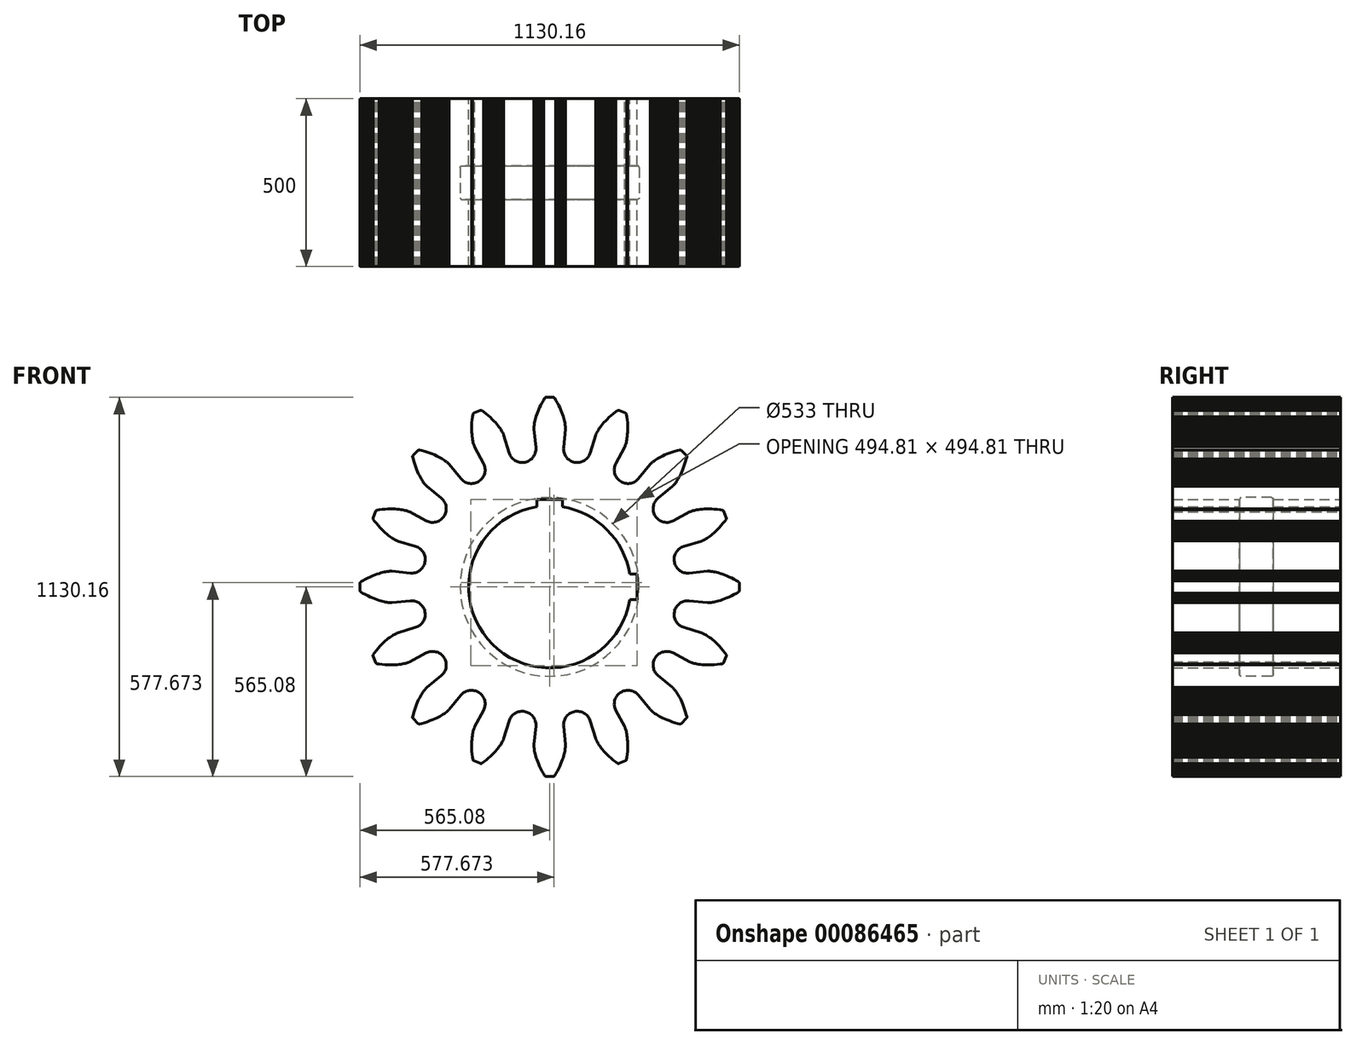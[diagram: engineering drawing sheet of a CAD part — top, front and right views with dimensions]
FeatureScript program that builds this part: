
annotation { "Feature Type Name" : "Feature", "Feature Type Description" : "" }
export const myFeature = defineFeature(function(context is Context, id is Id, definition is map)
    precondition{}
    {
        {
            var Q0;
            Q0=qCreatedBy(makeId("Front.planeOp"),FACE);
            var sketch = newSketch(context, id + "F0", { "sketchPlane" : qUnion([Q0])});
            skLineSegment(sketch, "E0", {"start": v(-415.34, 41.32) * mm, "end": v(-470.23, 46.78) * mm});
            skLineSegment(sketch, "E1", {"start": v(-470.23, 46.78) * mm, "end": v(-471.28, 46.9) * mm});
            skLineSegment(sketch, "E2", {"start": v(-471.28, 46.9) * mm, "end": v(-472.46, 46.9) * mm});
            skLineSegment(sketch, "E3", {"start": v(-472.46, 46.9) * mm, "end": v(-474.07, 46.85) * mm});
            skLineSegment(sketch, "E4", {"start": v(-474.07, 46.85) * mm, "end": v(-476.11, 46.73) * mm});
            skLineSegment(sketch, "E5", {"start": v(-476.11, 46.73) * mm, "end": v(-478.7, 46.56) * mm});
            skLineSegment(sketch, "E6", {"start": v(-478.7, 46.56) * mm, "end": v(-481.62, 46.2) * mm});
            skLineSegment(sketch, "E7", {"start": v(-481.62, 46.2) * mm, "end": v(-485.08, 45.8) * mm});
            skLineSegment(sketch, "E8", {"start": v(-485.08, 45.8) * mm, "end": v(-489, 45.12) * mm});
            skLineSegment(sketch, "E9", {"start": v(-489, 45.12) * mm, "end": v(-493.25, 44.26) * mm});
            skLineSegment(sketch, "E10", {"start": v(-493.25, 44.26) * mm, "end": v(-497.96, 43.13) * mm});
            skLineSegment(sketch, "E11", {"start": v(-497.96, 43.13) * mm, "end": v(-503.12, 41.82) * mm});
            skLineSegment(sketch, "E12", {"start": v(-503.12, 41.82) * mm, "end": v(-508.63, 40.13) * mm});
            skLineSegment(sketch, "E13", {"start": v(-508.63, 40.13) * mm, "end": v(-514.5, 38.14) * mm});
            skLineSegment(sketch, "E14", {"start": v(-514.5, 38.14) * mm, "end": v(-520.83, 35.78) * mm});
            skLineSegment(sketch, "E15", {"start": v(-520.83, 35.78) * mm, "end": v(-527.4, 33.12) * mm});
            skLineSegment(sketch, "E16", {"start": v(-527.4, 33.12) * mm, "end": v(-534.34, 30.07) * mm});
            skLineSegment(sketch, "E17", {"start": v(-534.34, 30.07) * mm, "end": v(-541.63, 26.62) * mm});
            skLineSegment(sketch, "E18", {"start": v(-541.63, 26.62) * mm, "end": v(-549.19, 22.67) * mm});
            skLineSegment(sketch, "E19", {"start": v(-549.19, 22.67) * mm, "end": v(-557, 18.31) * mm});
            skLineSegment(sketch, "E20", {"start": v(-557, 18.31) * mm, "end": v(-562.5, 15) * mm});
            skArc(sketch, "E21", {"start": v(-562.5, 15) * mm, "mid": v(-564.39, 13.06) * mm, "end": v(-565.08, 10.44) * mm});
            skLineSegment(sketch, "E22", {"start": v(-565.08, 10.44) * mm, "end": v(-565.08, -10.44) * mm});
            skArc(sketch, "E23", {"start": v(-565.08, -10.44) * mm, "mid": v(-564.39, -13.06) * mm, "end": v(-562.5, -15) * mm});
            skLineSegment(sketch, "E24", {"start": v(-562.5, -15) * mm, "end": v(-557, -18.31) * mm});
            skLineSegment(sketch, "E25", {"start": v(-557, -18.31) * mm, "end": v(-549.19, -22.67) * mm});
            skLineSegment(sketch, "E26", {"start": v(-549.19, -22.67) * mm, "end": v(-541.63, -26.62) * mm});
            skLineSegment(sketch, "E27", {"start": v(-541.63, -26.62) * mm, "end": v(-534.34, -30.07) * mm});
            skLineSegment(sketch, "E28", {"start": v(-534.34, -30.07) * mm, "end": v(-527.4, -33.12) * mm});
            skLineSegment(sketch, "E29", {"start": v(-527.4, -33.12) * mm, "end": v(-520.83, -35.78) * mm});
            skLineSegment(sketch, "E30", {"start": v(-520.83, -35.78) * mm, "end": v(-514.5, -38.14) * mm});
            skLineSegment(sketch, "E31", {"start": v(-514.5, -38.14) * mm, "end": v(-508.63, -40.13) * mm});
            skLineSegment(sketch, "E32", {"start": v(-508.63, -40.13) * mm, "end": v(-503.12, -41.82) * mm});
            skLineSegment(sketch, "E33", {"start": v(-503.12, -41.82) * mm, "end": v(-497.96, -43.13) * mm});
            skLineSegment(sketch, "E34", {"start": v(-497.96, -43.13) * mm, "end": v(-493.25, -44.26) * mm});
            skLineSegment(sketch, "E35", {"start": v(-493.25, -44.26) * mm, "end": v(-489, -45.12) * mm});
            skLineSegment(sketch, "E36", {"start": v(-489, -45.12) * mm, "end": v(-485.08, -45.8) * mm});
            skLineSegment(sketch, "E37", {"start": v(-485.08, -45.8) * mm, "end": v(-481.62, -46.2) * mm});
            skLineSegment(sketch, "E38", {"start": v(-481.62, -46.2) * mm, "end": v(-478.7, -46.56) * mm});
            skLineSegment(sketch, "E39", {"start": v(-478.7, -46.56) * mm, "end": v(-476.11, -46.73) * mm});
            skLineSegment(sketch, "E40", {"start": v(-476.11, -46.73) * mm, "end": v(-474.07, -46.85) * mm});
            skLineSegment(sketch, "E41", {"start": v(-474.07, -46.85) * mm, "end": v(-472.46, -46.9) * mm});
            skLineSegment(sketch, "E42", {"start": v(-472.46, -46.9) * mm, "end": v(-471.28, -46.9) * mm});
            skLineSegment(sketch, "E43", {"start": v(-471.28, -46.9) * mm, "end": v(-470.23, -46.78) * mm});
            skLineSegment(sketch, "E44", {"start": v(-470.23, -46.78) * mm, "end": v(-415.34, -41.32) * mm});
            skLineSegment(sketch, "E45", {"start": v(415.34, -41.32) * mm, "end": v(470.23, -46.78) * mm});
            skLineSegment(sketch, "E46", {"start": v(470.23, -46.78) * mm, "end": v(471.28, -46.9) * mm});
            skLineSegment(sketch, "E47", {"start": v(471.28, -46.9) * mm, "end": v(472.46, -46.9) * mm});
            skLineSegment(sketch, "E48", {"start": v(472.46, -46.9) * mm, "end": v(474.07, -46.85) * mm});
            skLineSegment(sketch, "E49", {"start": v(474.07, -46.85) * mm, "end": v(476.11, -46.73) * mm});
            skLineSegment(sketch, "E50", {"start": v(476.11, -46.73) * mm, "end": v(478.7, -46.56) * mm});
            skLineSegment(sketch, "E51", {"start": v(478.7, -46.56) * mm, "end": v(481.62, -46.2) * mm});
            skLineSegment(sketch, "E52", {"start": v(481.62, -46.2) * mm, "end": v(485.08, -45.8) * mm});
            skLineSegment(sketch, "E53", {"start": v(485.08, -45.8) * mm, "end": v(489, -45.12) * mm});
            skLineSegment(sketch, "E54", {"start": v(489, -45.12) * mm, "end": v(493.25, -44.26) * mm});
            skLineSegment(sketch, "E55", {"start": v(493.25, -44.26) * mm, "end": v(497.96, -43.13) * mm});
            skLineSegment(sketch, "E56", {"start": v(497.96, -43.13) * mm, "end": v(503.12, -41.82) * mm});
            skLineSegment(sketch, "E57", {"start": v(503.12, -41.82) * mm, "end": v(508.63, -40.13) * mm});
            skLineSegment(sketch, "E58", {"start": v(508.63, -40.13) * mm, "end": v(514.5, -38.14) * mm});
            skLineSegment(sketch, "E59", {"start": v(514.5, -38.14) * mm, "end": v(520.83, -35.78) * mm});
            skLineSegment(sketch, "E60", {"start": v(520.83, -35.78) * mm, "end": v(527.4, -33.12) * mm});
            skLineSegment(sketch, "E61", {"start": v(527.4, -33.12) * mm, "end": v(534.34, -30.07) * mm});
            skLineSegment(sketch, "E62", {"start": v(534.34, -30.07) * mm, "end": v(541.63, -26.62) * mm});
            skLineSegment(sketch, "E63", {"start": v(541.63, -26.62) * mm, "end": v(549.19, -22.67) * mm});
            skLineSegment(sketch, "E64", {"start": v(549.19, -22.67) * mm, "end": v(557, -18.31) * mm});
            skLineSegment(sketch, "E65", {"start": v(557, -18.31) * mm, "end": v(562.5, -15) * mm});
            skArc(sketch, "E66", {"start": v(562.5, -15) * mm, "mid": v(564.39, -13.06) * mm, "end": v(565.08, -10.44) * mm});
            skLineSegment(sketch, "E67", {"start": v(565.08, -10.44) * mm, "end": v(565.08, 10.44) * mm});
            skArc(sketch, "E68", {"start": v(565.08, 10.44) * mm, "mid": v(564.39, 13.06) * mm, "end": v(562.5, 15) * mm});
            skLineSegment(sketch, "E69", {"start": v(562.5, 15) * mm, "end": v(557, 18.31) * mm});
            skLineSegment(sketch, "E70", {"start": v(557, 18.31) * mm, "end": v(549.19, 22.67) * mm});
            skLineSegment(sketch, "E71", {"start": v(549.19, 22.67) * mm, "end": v(541.63, 26.62) * mm});
            skLineSegment(sketch, "E72", {"start": v(541.63, 26.62) * mm, "end": v(534.34, 30.07) * mm});
            skLineSegment(sketch, "E73", {"start": v(534.34, 30.07) * mm, "end": v(527.4, 33.12) * mm});
            skLineSegment(sketch, "E74", {"start": v(527.4, 33.12) * mm, "end": v(520.83, 35.78) * mm});
            skLineSegment(sketch, "E75", {"start": v(520.83, 35.78) * mm, "end": v(514.5, 38.14) * mm});
            skLineSegment(sketch, "E76", {"start": v(514.5, 38.14) * mm, "end": v(508.63, 40.13) * mm});
            skLineSegment(sketch, "E77", {"start": v(508.63, 40.13) * mm, "end": v(503.12, 41.82) * mm});
            skLineSegment(sketch, "E78", {"start": v(503.12, 41.82) * mm, "end": v(497.96, 43.13) * mm});
            skLineSegment(sketch, "E79", {"start": v(497.96, 43.13) * mm, "end": v(493.25, 44.26) * mm});
            skLineSegment(sketch, "E80", {"start": v(493.25, 44.26) * mm, "end": v(489, 45.12) * mm});
            skLineSegment(sketch, "E81", {"start": v(489, 45.12) * mm, "end": v(485.08, 45.8) * mm});
            skLineSegment(sketch, "E82", {"start": v(485.08, 45.8) * mm, "end": v(481.62, 46.2) * mm});
            skLineSegment(sketch, "E83", {"start": v(481.62, 46.2) * mm, "end": v(478.7, 46.56) * mm});
            skLineSegment(sketch, "E84", {"start": v(478.7, 46.56) * mm, "end": v(476.11, 46.73) * mm});
            skLineSegment(sketch, "E85", {"start": v(476.11, 46.73) * mm, "end": v(474.07, 46.85) * mm});
            skLineSegment(sketch, "E86", {"start": v(474.07, 46.85) * mm, "end": v(472.46, 46.9) * mm});
            skLineSegment(sketch, "E87", {"start": v(472.46, 46.9) * mm, "end": v(471.28, 46.9) * mm});
            skLineSegment(sketch, "E88", {"start": v(471.28, 46.9) * mm, "end": v(470.23, 46.78) * mm});
            skLineSegment(sketch, "E89", {"start": v(470.23, 46.78) * mm, "end": v(415.34, 41.32) * mm});
            skArc(sketch, "E90", {"start": v(371.58, -74.15) * mm, "mid": v(376.56, -102.85) * mm, "end": v(399.54, -120.77) * mm});
            skLineSegment(sketch, "E91", {"start": v(367.91, -197.12) * mm, "end": v(416.53, -223.17) * mm});
            skLineSegment(sketch, "E92", {"start": v(416.53, -223.17) * mm, "end": v(417.47, -223.67) * mm});
            skLineSegment(sketch, "E93", {"start": v(417.47, -223.67) * mm, "end": v(418.55, -224.13) * mm});
            skLineSegment(sketch, "E94", {"start": v(418.55, -224.13) * mm, "end": v(420.06, -224.7) * mm});
            skLineSegment(sketch, "E95", {"start": v(420.06, -224.7) * mm, "end": v(421.99, -225.37) * mm});
            skLineSegment(sketch, "E96", {"start": v(421.99, -225.37) * mm, "end": v(424.44, -226.2) * mm});
            skLineSegment(sketch, "E97", {"start": v(424.44, -226.2) * mm, "end": v(427.27, -227) * mm});
            skLineSegment(sketch, "E98", {"start": v(427.27, -227) * mm, "end": v(430.63, -227.95) * mm});
            skLineSegment(sketch, "E99", {"start": v(430.63, -227.95) * mm, "end": v(434.5, -228.82) * mm});
            skLineSegment(sketch, "E100", {"start": v(434.5, -228.82) * mm, "end": v(438.77, -229.65) * mm});
            skLineSegment(sketch, "E101", {"start": v(438.77, -229.65) * mm, "end": v(443.55, -230.4) * mm});
            skLineSegment(sketch, "E102", {"start": v(443.55, -230.4) * mm, "end": v(448.82, -231.18) * mm});
            skLineSegment(sketch, "E103", {"start": v(448.82, -231.18) * mm, "end": v(454.56, -231.72) * mm});
            skLineSegment(sketch, "E104", {"start": v(454.56, -231.72) * mm, "end": v(460.74, -232.13) * mm});
            skLineSegment(sketch, "E105", {"start": v(460.74, -232.13) * mm, "end": v(467.5, -232.37) * mm});
            skLineSegment(sketch, "E106", {"start": v(467.5, -232.37) * mm, "end": v(474.58, -232.43) * mm});
            skLineSegment(sketch, "E107", {"start": v(474.58, -232.43) * mm, "end": v(482.16, -232.26) * mm});
            skLineSegment(sketch, "E108", {"start": v(482.16, -232.26) * mm, "end": v(490.21, -231.87) * mm});
            skLineSegment(sketch, "E109", {"start": v(490.21, -231.87) * mm, "end": v(498.7, -231.1) * mm});
            skLineSegment(sketch, "E110", {"start": v(498.7, -231.1) * mm, "end": v(507.6, -230.07) * mm});
            skLineSegment(sketch, "E111", {"start": v(507.6, -230.07) * mm, "end": v(513.94, -229.12) * mm});
            skArc(sketch, "E112", {"start": v(513.94, -229.12) * mm, "mid": v(516.43, -228.05) * mm, "end": v(518.07, -225.9) * mm});
            skLineSegment(sketch, "E113", {"start": v(518.07, -225.9) * mm, "end": v(526.06, -206.6) * mm});
            skArc(sketch, "E114", {"start": v(526.06, -206.6) * mm, "mid": v(526.42, -203.92) * mm, "end": v(525.42, -201.4) * mm});
            skLineSegment(sketch, "E115", {"start": v(525.42, -201.4) * mm, "end": v(521.6, -196.24) * mm});
            skLineSegment(sketch, "E116", {"start": v(521.6, -196.24) * mm, "end": v(516.06, -189.22) * mm});
            skLineSegment(sketch, "E117", {"start": v(516.06, -189.22) * mm, "end": v(510.59, -182.68) * mm});
            skLineSegment(sketch, "E118", {"start": v(510.59, -182.68) * mm, "end": v(505.17, -176.7) * mm});
            skLineSegment(sketch, "E119", {"start": v(505.17, -176.7) * mm, "end": v(499.93, -171.23) * mm});
            skLineSegment(sketch, "E120", {"start": v(499.93, -171.23) * mm, "end": v(494.88, -166.26) * mm});
            skLineSegment(sketch, "E121", {"start": v(494.88, -166.26) * mm, "end": v(489.93, -161.65) * mm});
            skLineSegment(sketch, "E122", {"start": v(489.93, -161.65) * mm, "end": v(485.27, -157.57) * mm});
            skLineSegment(sketch, "E123", {"start": v(485.27, -157.57) * mm, "end": v(480.83, -153.9) * mm});
            skLineSegment(sketch, "E124", {"start": v(480.83, -153.9) * mm, "end": v(476.56, -150.72) * mm});
            skLineSegment(sketch, "E125", {"start": v(476.56, -150.72) * mm, "end": v(472.65, -147.86) * mm});
            skLineSegment(sketch, "E126", {"start": v(472.65, -147.86) * mm, "end": v(469.04, -145.44) * mm});
            skLineSegment(sketch, "E127", {"start": v(469.04, -145.44) * mm, "end": v(465.68, -143.32) * mm});
            skLineSegment(sketch, "E128", {"start": v(465.68, -143.32) * mm, "end": v(462.64, -141.62) * mm});
            skLineSegment(sketch, "E129", {"start": v(462.64, -141.62) * mm, "end": v(460.07, -140.17) * mm});
            skLineSegment(sketch, "E130", {"start": v(460.07, -140.17) * mm, "end": v(457.75, -139.03) * mm});
            skLineSegment(sketch, "E131", {"start": v(457.75, -139.03) * mm, "end": v(455.91, -138.14) * mm});
            skLineSegment(sketch, "E132", {"start": v(455.91, -138.14) * mm, "end": v(454.44, -137.47) * mm});
            skLineSegment(sketch, "E133", {"start": v(454.44, -137.47) * mm, "end": v(453.35, -137.03) * mm});
            skLineSegment(sketch, "E134", {"start": v(453.35, -137.03) * mm, "end": v(452.34, -136.72) * mm});
            skLineSegment(sketch, "E135", {"start": v(452.34, -136.72) * mm, "end": v(399.54, -120.77) * mm});
            skLineSegment(sketch, "E136", {"start": v(264.47, -322.91) * mm, "end": v(299.42, -365.58) * mm});
            skLineSegment(sketch, "E137", {"start": v(299.42, -365.58) * mm, "end": v(300.1, -366.4) * mm});
            skLineSegment(sketch, "E138", {"start": v(300.1, -366.4) * mm, "end": v(300.92, -367.24) * mm});
            skLineSegment(sketch, "E139", {"start": v(300.92, -367.24) * mm, "end": v(302.1, -368.34) * mm});
            skLineSegment(sketch, "E140", {"start": v(302.1, -368.34) * mm, "end": v(303.62, -369.7) * mm});
            skLineSegment(sketch, "E141", {"start": v(303.62, -369.7) * mm, "end": v(305.57, -371.41) * mm});
            skLineSegment(sketch, "E142", {"start": v(305.57, -371.41) * mm, "end": v(307.88, -373.23) * mm});
            skLineSegment(sketch, "E143", {"start": v(307.88, -373.23) * mm, "end": v(310.62, -375.4) * mm});
            skLineSegment(sketch, "E144", {"start": v(310.62, -375.4) * mm, "end": v(313.87, -377.68) * mm});
            skLineSegment(sketch, "E145", {"start": v(313.87, -377.68) * mm, "end": v(317.48, -380.08) * mm});
            skLineSegment(sketch, "E146", {"start": v(317.48, -380.08) * mm, "end": v(321.62, -382.61) * mm});
            skLineSegment(sketch, "E147", {"start": v(321.62, -382.61) * mm, "end": v(326.19, -385.33) * mm});
            skLineSegment(sketch, "E148", {"start": v(326.19, -385.33) * mm, "end": v(331.28, -388.03) * mm});
            skLineSegment(sketch, "E149", {"start": v(331.28, -388.03) * mm, "end": v(336.83, -390.78) * mm});
            skLineSegment(sketch, "E150", {"start": v(336.83, -390.78) * mm, "end": v(342.98, -393.58) * mm});
            skLineSegment(sketch, "E151", {"start": v(342.98, -393.58) * mm, "end": v(349.51, -396.35) * mm});
            skLineSegment(sketch, "E152", {"start": v(349.51, -396.35) * mm, "end": v(356.57, -399.1) * mm});
            skLineSegment(sketch, "E153", {"start": v(356.57, -399.1) * mm, "end": v(364.17, -401.81) * mm});
            skLineSegment(sketch, "E154", {"start": v(364.17, -401.81) * mm, "end": v(372.3, -404.36) * mm});
            skLineSegment(sketch, "E155", {"start": v(372.3, -404.36) * mm, "end": v(380.9, -406.8) * mm});
            skLineSegment(sketch, "E156", {"start": v(380.9, -406.8) * mm, "end": v(387.14, -408.35) * mm});
            skArc(sketch, "E157", {"start": v(387.14, -408.35) * mm, "mid": v(389.85, -408.32) * mm, "end": v(392.18, -406.95) * mm});
            skLineSegment(sketch, "E158", {"start": v(392.18, -406.95) * mm, "end": v(406.95, -392.18) * mm});
            skArc(sketch, "E159", {"start": v(406.95, -392.18) * mm, "mid": v(408.32, -389.85) * mm, "end": v(408.35, -387.14) * mm});
            skLineSegment(sketch, "E160", {"start": v(408.35, -387.14) * mm, "end": v(406.8, -380.9) * mm});
            skLineSegment(sketch, "E161", {"start": v(406.8, -380.9) * mm, "end": v(404.36, -372.3) * mm});
            skLineSegment(sketch, "E162", {"start": v(404.36, -372.3) * mm, "end": v(401.81, -364.17) * mm});
            skLineSegment(sketch, "E163", {"start": v(401.81, -364.17) * mm, "end": v(399.1, -356.57) * mm});
            skLineSegment(sketch, "E164", {"start": v(399.1, -356.57) * mm, "end": v(396.35, -349.51) * mm});
            skLineSegment(sketch, "E165", {"start": v(396.35, -349.51) * mm, "end": v(393.58, -342.98) * mm});
            skLineSegment(sketch, "E166", {"start": v(393.58, -342.98) * mm, "end": v(390.78, -336.83) * mm});
            skLineSegment(sketch, "E167", {"start": v(390.78, -336.83) * mm, "end": v(388.03, -331.28) * mm});
            skLineSegment(sketch, "E168", {"start": v(388.03, -331.28) * mm, "end": v(385.33, -326.19) * mm});
            skLineSegment(sketch, "E169", {"start": v(385.33, -326.19) * mm, "end": v(382.61, -321.62) * mm});
            skLineSegment(sketch, "E170", {"start": v(382.61, -321.62) * mm, "end": v(380.08, -317.48) * mm});
            skLineSegment(sketch, "E171", {"start": v(380.08, -317.48) * mm, "end": v(377.68, -313.87) * mm});
            skLineSegment(sketch, "E172", {"start": v(377.68, -313.87) * mm, "end": v(375.4, -310.62) * mm});
            skLineSegment(sketch, "E173", {"start": v(375.4, -310.62) * mm, "end": v(373.23, -307.88) * mm});
            skLineSegment(sketch, "E174", {"start": v(373.23, -307.88) * mm, "end": v(371.41, -305.57) * mm});
            skLineSegment(sketch, "E175", {"start": v(371.41, -305.57) * mm, "end": v(369.7, -303.62) * mm});
            skLineSegment(sketch, "E176", {"start": v(369.7, -303.62) * mm, "end": v(368.34, -302.1) * mm});
            skLineSegment(sketch, "E177", {"start": v(368.34, -302.1) * mm, "end": v(367.24, -300.92) * mm});
            skLineSegment(sketch, "E178", {"start": v(367.24, -300.92) * mm, "end": v(366.4, -300.1) * mm});
            skLineSegment(sketch, "E179", {"start": v(366.4, -300.1) * mm, "end": v(365.58, -299.42) * mm});
            skLineSegment(sketch, "E180", {"start": v(365.58, -299.42) * mm, "end": v(322.91, -264.47) * mm});
            skArc(sketch, "E181", {"start": v(415.34, -41.32) * mm, "mid": v(387.26, -49.08) * mm, "end": v(371.67, -73.7) * mm});
            skArc(sketch, "E182", {"start": v(120.77, -399.54) * mm, "mid": v(102.85, -376.56) * mm, "end": v(74.15, -371.58) * mm});
            skLineSegment(sketch, "E183", {"start": v(120.77, -399.54) * mm, "end": v(136.72, -452.34) * mm});
            skLineSegment(sketch, "E184", {"start": v(136.72, -452.34) * mm, "end": v(137.03, -453.35) * mm});
            skLineSegment(sketch, "E185", {"start": v(137.03, -453.35) * mm, "end": v(137.47, -454.44) * mm});
            skLineSegment(sketch, "E186", {"start": v(137.47, -454.44) * mm, "end": v(138.14, -455.91) * mm});
            skLineSegment(sketch, "E187", {"start": v(138.14, -455.91) * mm, "end": v(139.03, -457.75) * mm});
            skLineSegment(sketch, "E188", {"start": v(139.03, -457.75) * mm, "end": v(140.17, -460.07) * mm});
            skLineSegment(sketch, "E189", {"start": v(140.17, -460.07) * mm, "end": v(141.62, -462.64) * mm});
            skLineSegment(sketch, "E190", {"start": v(141.62, -462.64) * mm, "end": v(143.32, -465.68) * mm});
            skLineSegment(sketch, "E191", {"start": v(143.32, -465.68) * mm, "end": v(145.44, -469.04) * mm});
            skLineSegment(sketch, "E192", {"start": v(145.44, -469.04) * mm, "end": v(147.86, -472.65) * mm});
            skLineSegment(sketch, "E193", {"start": v(147.86, -472.65) * mm, "end": v(150.72, -476.56) * mm});
            skLineSegment(sketch, "E194", {"start": v(150.72, -476.56) * mm, "end": v(153.9, -480.83) * mm});
            skLineSegment(sketch, "E195", {"start": v(153.9, -480.83) * mm, "end": v(157.57, -485.27) * mm});
            skLineSegment(sketch, "E196", {"start": v(157.57, -485.27) * mm, "end": v(161.65, -489.93) * mm});
            skLineSegment(sketch, "E197", {"start": v(161.65, -489.93) * mm, "end": v(166.26, -494.88) * mm});
            skLineSegment(sketch, "E198", {"start": v(166.26, -494.88) * mm, "end": v(171.23, -499.93) * mm});
            skLineSegment(sketch, "E199", {"start": v(171.23, -499.93) * mm, "end": v(176.7, -505.17) * mm});
            skLineSegment(sketch, "E200", {"start": v(176.7, -505.17) * mm, "end": v(182.68, -510.59) * mm});
            skLineSegment(sketch, "E201", {"start": v(182.68, -510.59) * mm, "end": v(189.22, -516.06) * mm});
            skLineSegment(sketch, "E202", {"start": v(189.22, -516.06) * mm, "end": v(196.24, -521.6) * mm});
            skLineSegment(sketch, "E203", {"start": v(196.24, -521.6) * mm, "end": v(201.4, -525.42) * mm});
            skArc(sketch, "E204", {"start": v(201.4, -525.42) * mm, "mid": v(203.92, -526.42) * mm, "end": v(206.6, -526.06) * mm});
            skLineSegment(sketch, "E205", {"start": v(206.6, -526.06) * mm, "end": v(225.9, -518.07) * mm});
            skArc(sketch, "E206", {"start": v(225.9, -518.07) * mm, "mid": v(228.05, -516.43) * mm, "end": v(229.12, -513.94) * mm});
            skLineSegment(sketch, "E207", {"start": v(229.12, -513.94) * mm, "end": v(230.07, -507.6) * mm});
            skLineSegment(sketch, "E208", {"start": v(230.07, -507.6) * mm, "end": v(231.1, -498.7) * mm});
            skLineSegment(sketch, "E209", {"start": v(231.1, -498.7) * mm, "end": v(231.87, -490.21) * mm});
            skLineSegment(sketch, "E210", {"start": v(231.87, -490.21) * mm, "end": v(232.26, -482.16) * mm});
            skLineSegment(sketch, "E211", {"start": v(232.26, -482.16) * mm, "end": v(232.43, -474.58) * mm});
            skLineSegment(sketch, "E212", {"start": v(232.43, -474.58) * mm, "end": v(232.37, -467.5) * mm});
            skLineSegment(sketch, "E213", {"start": v(232.37, -467.5) * mm, "end": v(232.13, -460.74) * mm});
            skLineSegment(sketch, "E214", {"start": v(232.13, -460.74) * mm, "end": v(231.72, -454.56) * mm});
            skLineSegment(sketch, "E215", {"start": v(231.72, -454.56) * mm, "end": v(231.18, -448.82) * mm});
            skLineSegment(sketch, "E216", {"start": v(231.18, -448.82) * mm, "end": v(230.4, -443.55) * mm});
            skLineSegment(sketch, "E217", {"start": v(230.4, -443.55) * mm, "end": v(229.65, -438.77) * mm});
            skLineSegment(sketch, "E218", {"start": v(229.65, -438.77) * mm, "end": v(228.82, -434.5) * mm});
            skLineSegment(sketch, "E219", {"start": v(228.82, -434.5) * mm, "end": v(227.95, -430.63) * mm});
            skLineSegment(sketch, "E220", {"start": v(227.95, -430.63) * mm, "end": v(227, -427.27) * mm});
            skLineSegment(sketch, "E221", {"start": v(227, -427.27) * mm, "end": v(226.2, -424.44) * mm});
            skLineSegment(sketch, "E222", {"start": v(226.2, -424.44) * mm, "end": v(225.37, -421.99) * mm});
            skLineSegment(sketch, "E223", {"start": v(225.37, -421.99) * mm, "end": v(224.7, -420.06) * mm});
            skLineSegment(sketch, "E224", {"start": v(224.7, -420.06) * mm, "end": v(224.13, -418.55) * mm});
            skLineSegment(sketch, "E225", {"start": v(224.13, -418.55) * mm, "end": v(223.67, -417.47) * mm});
            skLineSegment(sketch, "E226", {"start": v(223.67, -417.47) * mm, "end": v(223.17, -416.53) * mm});
            skLineSegment(sketch, "E227", {"start": v(223.17, -416.53) * mm, "end": v(197.12, -367.91) * mm});
            skArc(sketch, "E228", {"start": v(73.7, -371.67) * mm, "mid": v(49.08, -387.26) * mm, "end": v(41.32, -415.34) * mm});
            skArc(sketch, "E229", {"start": v(-41.32, -415.34) * mm, "mid": v(-49.08, -387.26) * mm, "end": v(-73.7, -371.67) * mm});
            skArc(sketch, "E230", {"start": v(-74.15, -371.58) * mm, "mid": v(-102.85, -376.56) * mm, "end": v(-120.77, -399.54) * mm});
            skLineSegment(sketch, "E231", {"start": v(-197.12, -367.91) * mm, "end": v(-223.17, -416.53) * mm});
            skLineSegment(sketch, "E232", {"start": v(-223.17, -416.53) * mm, "end": v(-223.67, -417.47) * mm});
            skLineSegment(sketch, "E233", {"start": v(-223.67, -417.47) * mm, "end": v(-224.13, -418.55) * mm});
            skLineSegment(sketch, "E234", {"start": v(-224.13, -418.55) * mm, "end": v(-224.7, -420.06) * mm});
            skLineSegment(sketch, "E235", {"start": v(-224.7, -420.06) * mm, "end": v(-225.37, -421.99) * mm});
            skLineSegment(sketch, "E236", {"start": v(-225.37, -421.99) * mm, "end": v(-226.2, -424.44) * mm});
            skLineSegment(sketch, "E237", {"start": v(-226.2, -424.44) * mm, "end": v(-227, -427.27) * mm});
            skLineSegment(sketch, "E238", {"start": v(-227, -427.27) * mm, "end": v(-227.95, -430.63) * mm});
            skLineSegment(sketch, "E239", {"start": v(-227.95, -430.63) * mm, "end": v(-228.82, -434.5) * mm});
            skLineSegment(sketch, "E240", {"start": v(-228.82, -434.5) * mm, "end": v(-229.65, -438.77) * mm});
            skLineSegment(sketch, "E241", {"start": v(-229.65, -438.77) * mm, "end": v(-230.4, -443.55) * mm});
            skLineSegment(sketch, "E242", {"start": v(-230.4, -443.55) * mm, "end": v(-231.18, -448.82) * mm});
            skLineSegment(sketch, "E243", {"start": v(-231.18, -448.82) * mm, "end": v(-231.72, -454.56) * mm});
            skLineSegment(sketch, "E244", {"start": v(-231.72, -454.56) * mm, "end": v(-232.13, -460.74) * mm});
            skLineSegment(sketch, "E245", {"start": v(-232.13, -460.74) * mm, "end": v(-232.37, -467.5) * mm});
            skLineSegment(sketch, "E246", {"start": v(-232.37, -467.5) * mm, "end": v(-232.43, -474.58) * mm});
            skLineSegment(sketch, "E247", {"start": v(-232.43, -474.58) * mm, "end": v(-232.26, -482.16) * mm});
            skLineSegment(sketch, "E248", {"start": v(-232.26, -482.16) * mm, "end": v(-231.87, -490.21) * mm});
            skLineSegment(sketch, "E249", {"start": v(-231.87, -490.21) * mm, "end": v(-231.1, -498.7) * mm});
            skLineSegment(sketch, "E250", {"start": v(-231.1, -498.7) * mm, "end": v(-230.07, -507.6) * mm});
            skLineSegment(sketch, "E251", {"start": v(-230.07, -507.6) * mm, "end": v(-229.12, -513.94) * mm});
            skArc(sketch, "E252", {"start": v(-229.12, -513.94) * mm, "mid": v(-228.05, -516.43) * mm, "end": v(-225.9, -518.07) * mm});
            skLineSegment(sketch, "E253", {"start": v(-225.9, -518.07) * mm, "end": v(-206.6, -526.06) * mm});
            skArc(sketch, "E254", {"start": v(-206.6, -526.06) * mm, "mid": v(-203.92, -526.42) * mm, "end": v(-201.4, -525.42) * mm});
            skLineSegment(sketch, "E255", {"start": v(-201.4, -525.42) * mm, "end": v(-196.24, -521.6) * mm});
            skLineSegment(sketch, "E256", {"start": v(-196.24, -521.6) * mm, "end": v(-189.22, -516.06) * mm});
            skLineSegment(sketch, "E257", {"start": v(-189.22, -516.06) * mm, "end": v(-182.68, -510.59) * mm});
            skLineSegment(sketch, "E258", {"start": v(-182.68, -510.59) * mm, "end": v(-176.7, -505.17) * mm});
            skLineSegment(sketch, "E259", {"start": v(-176.7, -505.17) * mm, "end": v(-171.23, -499.93) * mm});
            skLineSegment(sketch, "E260", {"start": v(-171.23, -499.93) * mm, "end": v(-166.26, -494.88) * mm});
            skLineSegment(sketch, "E261", {"start": v(-166.26, -494.88) * mm, "end": v(-161.65, -489.93) * mm});
            skLineSegment(sketch, "E262", {"start": v(-161.65, -489.93) * mm, "end": v(-157.57, -485.27) * mm});
            skLineSegment(sketch, "E263", {"start": v(-157.57, -485.27) * mm, "end": v(-153.9, -480.83) * mm});
            skLineSegment(sketch, "E264", {"start": v(-153.9, -480.83) * mm, "end": v(-150.72, -476.56) * mm});
            skLineSegment(sketch, "E265", {"start": v(-150.72, -476.56) * mm, "end": v(-147.86, -472.65) * mm});
            skLineSegment(sketch, "E266", {"start": v(-147.86, -472.65) * mm, "end": v(-145.44, -469.04) * mm});
            skLineSegment(sketch, "E267", {"start": v(-145.44, -469.04) * mm, "end": v(-143.32, -465.68) * mm});
            skLineSegment(sketch, "E268", {"start": v(-143.32, -465.68) * mm, "end": v(-141.62, -462.64) * mm});
            skLineSegment(sketch, "E269", {"start": v(-141.62, -462.64) * mm, "end": v(-140.17, -460.07) * mm});
            skLineSegment(sketch, "E270", {"start": v(-140.17, -460.07) * mm, "end": v(-139.03, -457.75) * mm});
            skLineSegment(sketch, "E271", {"start": v(-139.03, -457.75) * mm, "end": v(-138.14, -455.91) * mm});
            skLineSegment(sketch, "E272", {"start": v(-138.14, -455.91) * mm, "end": v(-137.47, -454.44) * mm});
            skLineSegment(sketch, "E273", {"start": v(-137.47, -454.44) * mm, "end": v(-137.03, -453.35) * mm});
            skLineSegment(sketch, "E274", {"start": v(-137.03, -453.35) * mm, "end": v(-136.72, -452.34) * mm});
            skLineSegment(sketch, "E275", {"start": v(-136.72, -452.34) * mm, "end": v(-120.77, -399.54) * mm});
            skLineSegment(sketch, "E276", {"start": v(-322.91, -264.47) * mm, "end": v(-365.58, -299.42) * mm});
            skLineSegment(sketch, "E277", {"start": v(-365.58, -299.42) * mm, "end": v(-366.4, -300.1) * mm});
            skLineSegment(sketch, "E278", {"start": v(-366.4, -300.1) * mm, "end": v(-367.24, -300.92) * mm});
            skLineSegment(sketch, "E279", {"start": v(-367.24, -300.92) * mm, "end": v(-368.34, -302.1) * mm});
            skLineSegment(sketch, "E280", {"start": v(-368.34, -302.1) * mm, "end": v(-369.7, -303.62) * mm});
            skLineSegment(sketch, "E281", {"start": v(-369.7, -303.62) * mm, "end": v(-371.41, -305.57) * mm});
            skLineSegment(sketch, "E282", {"start": v(-371.41, -305.57) * mm, "end": v(-373.23, -307.88) * mm});
            skLineSegment(sketch, "E283", {"start": v(-373.23, -307.88) * mm, "end": v(-375.4, -310.62) * mm});
            skLineSegment(sketch, "E284", {"start": v(-375.4, -310.62) * mm, "end": v(-377.68, -313.87) * mm});
            skLineSegment(sketch, "E285", {"start": v(-377.68, -313.87) * mm, "end": v(-380.08, -317.48) * mm});
            skLineSegment(sketch, "E286", {"start": v(-380.08, -317.48) * mm, "end": v(-382.61, -321.62) * mm});
            skLineSegment(sketch, "E287", {"start": v(-382.61, -321.62) * mm, "end": v(-385.33, -326.19) * mm});
            skLineSegment(sketch, "E288", {"start": v(-385.33, -326.19) * mm, "end": v(-388.03, -331.28) * mm});
            skLineSegment(sketch, "E289", {"start": v(-388.03, -331.28) * mm, "end": v(-390.78, -336.83) * mm});
            skLineSegment(sketch, "E290", {"start": v(-390.78, -336.83) * mm, "end": v(-393.58, -342.98) * mm});
            skLineSegment(sketch, "E291", {"start": v(-393.58, -342.98) * mm, "end": v(-396.35, -349.51) * mm});
            skLineSegment(sketch, "E292", {"start": v(-396.35, -349.51) * mm, "end": v(-399.1, -356.57) * mm});
            skLineSegment(sketch, "E293", {"start": v(-399.1, -356.57) * mm, "end": v(-401.81, -364.17) * mm});
            skLineSegment(sketch, "E294", {"start": v(-401.81, -364.17) * mm, "end": v(-404.36, -372.3) * mm});
            skLineSegment(sketch, "E295", {"start": v(-404.36, -372.3) * mm, "end": v(-406.8, -380.9) * mm});
            skLineSegment(sketch, "E296", {"start": v(-406.8, -380.9) * mm, "end": v(-408.35, -387.14) * mm});
            skArc(sketch, "E297", {"start": v(-408.35, -387.14) * mm, "mid": v(-408.32, -389.85) * mm, "end": v(-406.95, -392.18) * mm});
            skLineSegment(sketch, "E298", {"start": v(-406.95, -392.18) * mm, "end": v(-392.18, -406.95) * mm});
            skArc(sketch, "E299", {"start": v(-392.18, -406.95) * mm, "mid": v(-389.85, -408.32) * mm, "end": v(-387.14, -408.35) * mm});
            skLineSegment(sketch, "E300", {"start": v(-387.14, -408.35) * mm, "end": v(-380.9, -406.8) * mm});
            skLineSegment(sketch, "E301", {"start": v(-380.9, -406.8) * mm, "end": v(-372.3, -404.36) * mm});
            skLineSegment(sketch, "E302", {"start": v(-372.3, -404.36) * mm, "end": v(-364.17, -401.81) * mm});
            skLineSegment(sketch, "E303", {"start": v(-364.17, -401.81) * mm, "end": v(-356.57, -399.1) * mm});
            skLineSegment(sketch, "E304", {"start": v(-356.57, -399.1) * mm, "end": v(-349.51, -396.35) * mm});
            skLineSegment(sketch, "E305", {"start": v(-349.51, -396.35) * mm, "end": v(-342.98, -393.58) * mm});
            skLineSegment(sketch, "E306", {"start": v(-342.98, -393.58) * mm, "end": v(-336.83, -390.78) * mm});
            skLineSegment(sketch, "E307", {"start": v(-336.83, -390.78) * mm, "end": v(-331.28, -388.03) * mm});
            skLineSegment(sketch, "E308", {"start": v(-331.28, -388.03) * mm, "end": v(-326.19, -385.33) * mm});
            skLineSegment(sketch, "E309", {"start": v(-326.19, -385.33) * mm, "end": v(-321.62, -382.61) * mm});
            skLineSegment(sketch, "E310", {"start": v(-321.62, -382.61) * mm, "end": v(-317.48, -380.08) * mm});
            skLineSegment(sketch, "E311", {"start": v(-317.48, -380.08) * mm, "end": v(-313.87, -377.68) * mm});
            skLineSegment(sketch, "E312", {"start": v(-313.87, -377.68) * mm, "end": v(-310.62, -375.4) * mm});
            skLineSegment(sketch, "E313", {"start": v(-310.62, -375.4) * mm, "end": v(-307.88, -373.23) * mm});
            skLineSegment(sketch, "E314", {"start": v(-307.88, -373.23) * mm, "end": v(-305.57, -371.41) * mm});
            skLineSegment(sketch, "E315", {"start": v(-305.57, -371.41) * mm, "end": v(-303.62, -369.7) * mm});
            skLineSegment(sketch, "E316", {"start": v(-303.62, -369.7) * mm, "end": v(-302.1, -368.34) * mm});
            skLineSegment(sketch, "E317", {"start": v(-302.1, -368.34) * mm, "end": v(-300.92, -367.24) * mm});
            skLineSegment(sketch, "E318", {"start": v(-300.92, -367.24) * mm, "end": v(-300.1, -366.4) * mm});
            skLineSegment(sketch, "E319", {"start": v(-300.1, -366.4) * mm, "end": v(-299.42, -365.58) * mm});
            skLineSegment(sketch, "E320", {"start": v(-299.42, -365.58) * mm, "end": v(-264.47, -322.91) * mm});
            skLineSegment(sketch, "E321", {"start": v(-41.32, -415.34) * mm, "end": v(-46.78, -470.23) * mm});
            skLineSegment(sketch, "E322", {"start": v(-46.78, -470.23) * mm, "end": v(-46.9, -471.28) * mm});
            skLineSegment(sketch, "E323", {"start": v(-46.9, -471.28) * mm, "end": v(-46.9, -472.46) * mm});
            skLineSegment(sketch, "E324", {"start": v(-46.9, -472.46) * mm, "end": v(-46.85, -474.07) * mm});
            skLineSegment(sketch, "E325", {"start": v(-46.85, -474.07) * mm, "end": v(-46.73, -476.11) * mm});
            skLineSegment(sketch, "E326", {"start": v(-46.73, -476.11) * mm, "end": v(-46.56, -478.7) * mm});
            skLineSegment(sketch, "E327", {"start": v(-46.56, -478.7) * mm, "end": v(-46.2, -481.62) * mm});
            skLineSegment(sketch, "E328", {"start": v(-46.2, -481.62) * mm, "end": v(-45.8, -485.08) * mm});
            skLineSegment(sketch, "E329", {"start": v(-45.8, -485.08) * mm, "end": v(-45.12, -489) * mm});
            skLineSegment(sketch, "E330", {"start": v(-45.12, -489) * mm, "end": v(-44.26, -493.25) * mm});
            skLineSegment(sketch, "E331", {"start": v(-44.26, -493.25) * mm, "end": v(-43.13, -497.96) * mm});
            skLineSegment(sketch, "E332", {"start": v(-43.13, -497.96) * mm, "end": v(-41.82, -503.12) * mm});
            skLineSegment(sketch, "E333", {"start": v(-41.82, -503.12) * mm, "end": v(-40.13, -508.63) * mm});
            skLineSegment(sketch, "E334", {"start": v(-40.13, -508.63) * mm, "end": v(-38.14, -514.5) * mm});
            skLineSegment(sketch, "E335", {"start": v(-38.14, -514.5) * mm, "end": v(-35.78, -520.83) * mm});
            skLineSegment(sketch, "E336", {"start": v(-35.78, -520.83) * mm, "end": v(-33.12, -527.4) * mm});
            skLineSegment(sketch, "E337", {"start": v(-33.12, -527.4) * mm, "end": v(-30.07, -534.34) * mm});
            skLineSegment(sketch, "E338", {"start": v(-30.07, -534.34) * mm, "end": v(-26.62, -541.63) * mm});
            skLineSegment(sketch, "E339", {"start": v(-26.62, -541.63) * mm, "end": v(-22.67, -549.19) * mm});
            skLineSegment(sketch, "E340", {"start": v(-22.67, -549.19) * mm, "end": v(-18.31, -557) * mm});
            skLineSegment(sketch, "E341", {"start": v(-18.31, -557) * mm, "end": v(-15, -562.5) * mm});
            skArc(sketch, "E342", {"start": v(-15, -562.5) * mm, "mid": v(-13.06, -564.39) * mm, "end": v(-10.44, -565.08) * mm});
            skLineSegment(sketch, "E343", {"start": v(-10.44, -565.08) * mm, "end": v(10.44, -565.08) * mm});
            skArc(sketch, "E344", {"start": v(10.44, -565.08) * mm, "mid": v(13.06, -564.39) * mm, "end": v(15, -562.5) * mm});
            skLineSegment(sketch, "E345", {"start": v(15, -562.5) * mm, "end": v(18.31, -557) * mm});
            skLineSegment(sketch, "E346", {"start": v(18.31, -557) * mm, "end": v(22.67, -549.19) * mm});
            skLineSegment(sketch, "E347", {"start": v(22.67, -549.19) * mm, "end": v(26.62, -541.63) * mm});
            skLineSegment(sketch, "E348", {"start": v(26.62, -541.63) * mm, "end": v(30.07, -534.34) * mm});
            skLineSegment(sketch, "E349", {"start": v(30.07, -534.34) * mm, "end": v(33.12, -527.4) * mm});
            skLineSegment(sketch, "E350", {"start": v(33.12, -527.4) * mm, "end": v(35.78, -520.83) * mm});
            skLineSegment(sketch, "E351", {"start": v(35.78, -520.83) * mm, "end": v(38.14, -514.5) * mm});
            skLineSegment(sketch, "E352", {"start": v(38.14, -514.5) * mm, "end": v(40.13, -508.63) * mm});
            skLineSegment(sketch, "E353", {"start": v(40.13, -508.63) * mm, "end": v(41.82, -503.12) * mm});
            skLineSegment(sketch, "E354", {"start": v(41.82, -503.12) * mm, "end": v(43.13, -497.96) * mm});
            skLineSegment(sketch, "E355", {"start": v(43.13, -497.96) * mm, "end": v(44.26, -493.25) * mm});
            skLineSegment(sketch, "E356", {"start": v(44.26, -493.25) * mm, "end": v(45.12, -489) * mm});
            skLineSegment(sketch, "E357", {"start": v(45.12, -489) * mm, "end": v(45.8, -485.08) * mm});
            skLineSegment(sketch, "E358", {"start": v(45.8, -485.08) * mm, "end": v(46.2, -481.62) * mm});
            skLineSegment(sketch, "E359", {"start": v(46.2, -481.62) * mm, "end": v(46.56, -478.7) * mm});
            skLineSegment(sketch, "E360", {"start": v(46.56, -478.7) * mm, "end": v(46.73, -476.11) * mm});
            skLineSegment(sketch, "E361", {"start": v(46.73, -476.11) * mm, "end": v(46.85, -474.07) * mm});
            skLineSegment(sketch, "E362", {"start": v(46.85, -474.07) * mm, "end": v(46.9, -472.46) * mm});
            skLineSegment(sketch, "E363", {"start": v(46.9, -472.46) * mm, "end": v(46.9, -471.28) * mm});
            skLineSegment(sketch, "E364", {"start": v(46.9, -471.28) * mm, "end": v(46.78, -470.23) * mm});
            skLineSegment(sketch, "E365", {"start": v(46.78, -470.23) * mm, "end": v(41.32, -415.34) * mm});
            skLineSegment(sketch, "E366", {"start": v(-399.54, -120.77) * mm, "end": v(-452.34, -136.72) * mm});
            skLineSegment(sketch, "E367", {"start": v(-452.34, -136.72) * mm, "end": v(-453.35, -137.03) * mm});
            skLineSegment(sketch, "E368", {"start": v(-453.35, -137.03) * mm, "end": v(-454.44, -137.47) * mm});
            skLineSegment(sketch, "E369", {"start": v(-454.44, -137.47) * mm, "end": v(-455.91, -138.14) * mm});
            skLineSegment(sketch, "E370", {"start": v(-455.91, -138.14) * mm, "end": v(-457.75, -139.03) * mm});
            skLineSegment(sketch, "E371", {"start": v(-457.75, -139.03) * mm, "end": v(-460.07, -140.17) * mm});
            skLineSegment(sketch, "E372", {"start": v(-460.07, -140.17) * mm, "end": v(-462.64, -141.62) * mm});
            skLineSegment(sketch, "E373", {"start": v(-462.64, -141.62) * mm, "end": v(-465.68, -143.32) * mm});
            skLineSegment(sketch, "E374", {"start": v(-465.68, -143.32) * mm, "end": v(-469.04, -145.44) * mm});
            skLineSegment(sketch, "E375", {"start": v(-469.04, -145.44) * mm, "end": v(-472.65, -147.86) * mm});
            skLineSegment(sketch, "E376", {"start": v(-472.65, -147.86) * mm, "end": v(-476.56, -150.72) * mm});
            skLineSegment(sketch, "E377", {"start": v(-476.56, -150.72) * mm, "end": v(-480.83, -153.9) * mm});
            skLineSegment(sketch, "E378", {"start": v(-480.83, -153.9) * mm, "end": v(-485.27, -157.57) * mm});
            skLineSegment(sketch, "E379", {"start": v(-485.27, -157.57) * mm, "end": v(-489.93, -161.65) * mm});
            skLineSegment(sketch, "E380", {"start": v(-489.93, -161.65) * mm, "end": v(-494.88, -166.26) * mm});
            skLineSegment(sketch, "E381", {"start": v(-494.88, -166.26) * mm, "end": v(-499.93, -171.23) * mm});
            skLineSegment(sketch, "E382", {"start": v(-499.93, -171.23) * mm, "end": v(-505.17, -176.7) * mm});
            skLineSegment(sketch, "E383", {"start": v(-505.17, -176.7) * mm, "end": v(-510.59, -182.68) * mm});
            skLineSegment(sketch, "E384", {"start": v(-510.59, -182.68) * mm, "end": v(-516.06, -189.22) * mm});
            skLineSegment(sketch, "E385", {"start": v(-516.06, -189.22) * mm, "end": v(-521.6, -196.24) * mm});
            skLineSegment(sketch, "E386", {"start": v(-521.6, -196.24) * mm, "end": v(-525.42, -201.4) * mm});
            skArc(sketch, "E387", {"start": v(-525.42, -201.4) * mm, "mid": v(-526.42, -203.92) * mm, "end": v(-526.06, -206.6) * mm});
            skLineSegment(sketch, "E388", {"start": v(-526.06, -206.6) * mm, "end": v(-518.07, -225.9) * mm});
            skArc(sketch, "E389", {"start": v(-518.07, -225.9) * mm, "mid": v(-516.43, -228.05) * mm, "end": v(-513.94, -229.12) * mm});
            skLineSegment(sketch, "E390", {"start": v(-513.94, -229.12) * mm, "end": v(-507.6, -230.07) * mm});
            skLineSegment(sketch, "E391", {"start": v(-507.6, -230.07) * mm, "end": v(-498.7, -231.1) * mm});
            skLineSegment(sketch, "E392", {"start": v(-498.7, -231.1) * mm, "end": v(-490.21, -231.87) * mm});
            skLineSegment(sketch, "E393", {"start": v(-490.21, -231.87) * mm, "end": v(-482.16, -232.26) * mm});
            skLineSegment(sketch, "E394", {"start": v(-482.16, -232.26) * mm, "end": v(-474.58, -232.43) * mm});
            skLineSegment(sketch, "E395", {"start": v(-474.58, -232.43) * mm, "end": v(-467.5, -232.37) * mm});
            skLineSegment(sketch, "E396", {"start": v(-467.5, -232.37) * mm, "end": v(-460.74, -232.13) * mm});
            skLineSegment(sketch, "E397", {"start": v(-460.74, -232.13) * mm, "end": v(-454.56, -231.72) * mm});
            skLineSegment(sketch, "E398", {"start": v(-454.56, -231.72) * mm, "end": v(-448.82, -231.18) * mm});
            skLineSegment(sketch, "E399", {"start": v(-448.82, -231.18) * mm, "end": v(-443.55, -230.4) * mm});
            skLineSegment(sketch, "E400", {"start": v(-443.55, -230.4) * mm, "end": v(-438.77, -229.65) * mm});
            skLineSegment(sketch, "E401", {"start": v(-438.77, -229.65) * mm, "end": v(-434.5, -228.82) * mm});
            skLineSegment(sketch, "E402", {"start": v(-434.5, -228.82) * mm, "end": v(-430.63, -227.95) * mm});
            skLineSegment(sketch, "E403", {"start": v(-430.63, -227.95) * mm, "end": v(-427.27, -227) * mm});
            skLineSegment(sketch, "E404", {"start": v(-427.27, -227) * mm, "end": v(-424.44, -226.2) * mm});
            skLineSegment(sketch, "E405", {"start": v(-424.44, -226.2) * mm, "end": v(-421.99, -225.37) * mm});
            skLineSegment(sketch, "E406", {"start": v(-421.99, -225.37) * mm, "end": v(-420.06, -224.7) * mm});
            skLineSegment(sketch, "E407", {"start": v(-420.06, -224.7) * mm, "end": v(-418.55, -224.13) * mm});
            skLineSegment(sketch, "E408", {"start": v(-418.55, -224.13) * mm, "end": v(-417.47, -223.67) * mm});
            skLineSegment(sketch, "E409", {"start": v(-417.47, -223.67) * mm, "end": v(-416.53, -223.17) * mm});
            skLineSegment(sketch, "E410", {"start": v(-416.53, -223.17) * mm, "end": v(-367.91, -197.12) * mm});
            skArc(sketch, "E411", {"start": v(367.91, -197.12) * mm, "mid": v(339, -193.54) * mm, "end": v(315.18, -210.32) * mm});
            skArc(sketch, "E412", {"start": v(-315.18, -210.32) * mm, "mid": v(-339, -193.54) * mm, "end": v(-367.91, -197.12) * mm});
            skArc(sketch, "E413", {"start": v(-210.7, -314.92) * mm, "mid": v(-239.13, -308.53) * mm, "end": v(-264.47, -322.91) * mm});
            skArc(sketch, "E414", {"start": v(-197.12, -367.91) * mm, "mid": v(-193.54, -339) * mm, "end": v(-210.32, -315.18) * mm});
            skLineSegment(sketch, "E415", {"start": v(-73.7, -371.67) * mm, "end": v(-74.15, -371.58) * mm});
            skLineSegment(sketch, "E416", {"start": v(-210.32, -315.18) * mm, "end": v(-210.7, -314.92) * mm});
            skArc(sketch, "E417", {"start": v(-322.91, -264.47) * mm, "mid": v(-308.53, -239.13) * mm, "end": v(-314.92, -210.7) * mm});
            skLineSegment(sketch, "E418", {"start": v(-314.92, -210.7) * mm, "end": v(-315.18, -210.32) * mm});
            skLineSegment(sketch, "E419", {"start": v(74.15, -371.58) * mm, "end": v(73.7, -371.67) * mm});
            skArc(sketch, "E420", {"start": v(210.32, -315.18) * mm, "mid": v(193.54, -339) * mm, "end": v(197.12, -367.91) * mm});
            skArc(sketch, "E421", {"start": v(264.47, -322.91) * mm, "mid": v(239.13, -308.53) * mm, "end": v(210.7, -314.92) * mm});
            skLineSegment(sketch, "E422", {"start": v(210.7, -314.92) * mm, "end": v(210.32, -315.18) * mm});
            skArc(sketch, "E423", {"start": v(314.92, -210.7) * mm, "mid": v(308.53, -239.13) * mm, "end": v(322.91, -264.47) * mm});
            skLineSegment(sketch, "E424", {"start": v(315.18, -210.32) * mm, "end": v(314.92, -210.7) * mm});
            skArc(sketch, "E425", {"start": v(-399.54, -120.77) * mm, "mid": v(-376.56, -102.85) * mm, "end": v(-371.58, -74.15) * mm});
            skArc(sketch, "E426", {"start": v(-371.67, -73.7) * mm, "mid": v(-387.26, -49.08) * mm, "end": v(-415.34, -41.32) * mm});
            skLineSegment(sketch, "E427", {"start": v(-371.58, -74.15) * mm, "end": v(-371.67, -73.7) * mm});
            skLineSegment(sketch, "E428", {"start": v(371.67, -73.7) * mm, "end": v(371.58, -74.15) * mm});
            skLineSegment(sketch, "E429", {"start": v(322.91, 264.47) * mm, "end": v(365.58, 299.42) * mm});
            skLineSegment(sketch, "E430", {"start": v(365.58, 299.42) * mm, "end": v(366.4, 300.1) * mm});
            skLineSegment(sketch, "E431", {"start": v(366.4, 300.1) * mm, "end": v(367.24, 300.92) * mm});
            skLineSegment(sketch, "E432", {"start": v(367.24, 300.92) * mm, "end": v(368.34, 302.1) * mm});
            skLineSegment(sketch, "E433", {"start": v(368.34, 302.1) * mm, "end": v(369.7, 303.62) * mm});
            skLineSegment(sketch, "E434", {"start": v(369.7, 303.62) * mm, "end": v(371.41, 305.57) * mm});
            skLineSegment(sketch, "E435", {"start": v(371.41, 305.57) * mm, "end": v(373.23, 307.88) * mm});
            skLineSegment(sketch, "E436", {"start": v(373.23, 307.88) * mm, "end": v(375.4, 310.62) * mm});
            skLineSegment(sketch, "E437", {"start": v(375.4, 310.62) * mm, "end": v(377.68, 313.87) * mm});
            skLineSegment(sketch, "E438", {"start": v(377.68, 313.87) * mm, "end": v(380.08, 317.48) * mm});
            skLineSegment(sketch, "E439", {"start": v(380.08, 317.48) * mm, "end": v(382.61, 321.62) * mm});
            skLineSegment(sketch, "E440", {"start": v(382.61, 321.62) * mm, "end": v(385.33, 326.19) * mm});
            skLineSegment(sketch, "E441", {"start": v(385.33, 326.19) * mm, "end": v(388.03, 331.28) * mm});
            skLineSegment(sketch, "E442", {"start": v(388.03, 331.28) * mm, "end": v(390.78, 336.83) * mm});
            skLineSegment(sketch, "E443", {"start": v(390.78, 336.83) * mm, "end": v(393.58, 342.98) * mm});
            skLineSegment(sketch, "E444", {"start": v(393.58, 342.98) * mm, "end": v(396.35, 349.51) * mm});
            skLineSegment(sketch, "E445", {"start": v(396.35, 349.51) * mm, "end": v(399.1, 356.57) * mm});
            skLineSegment(sketch, "E446", {"start": v(399.1, 356.57) * mm, "end": v(401.81, 364.17) * mm});
            skLineSegment(sketch, "E447", {"start": v(401.81, 364.17) * mm, "end": v(404.36, 372.3) * mm});
            skLineSegment(sketch, "E448", {"start": v(404.36, 372.3) * mm, "end": v(406.8, 380.9) * mm});
            skLineSegment(sketch, "E449", {"start": v(406.8, 380.9) * mm, "end": v(408.35, 387.14) * mm});
            skArc(sketch, "E450", {"start": v(408.35, 387.14) * mm, "mid": v(408.32, 389.85) * mm, "end": v(406.95, 392.18) * mm});
            skLineSegment(sketch, "E451", {"start": v(406.95, 392.18) * mm, "end": v(392.18, 406.95) * mm});
            skArc(sketch, "E452", {"start": v(392.18, 406.95) * mm, "mid": v(389.85, 408.32) * mm, "end": v(387.14, 408.35) * mm});
            skLineSegment(sketch, "E453", {"start": v(387.14, 408.35) * mm, "end": v(380.9, 406.8) * mm});
            skLineSegment(sketch, "E454", {"start": v(380.9, 406.8) * mm, "end": v(372.3, 404.36) * mm});
            skLineSegment(sketch, "E455", {"start": v(372.3, 404.36) * mm, "end": v(364.17, 401.81) * mm});
            skLineSegment(sketch, "E456", {"start": v(364.17, 401.81) * mm, "end": v(356.57, 399.1) * mm});
            skLineSegment(sketch, "E457", {"start": v(356.57, 399.1) * mm, "end": v(349.51, 396.35) * mm});
            skLineSegment(sketch, "E458", {"start": v(349.51, 396.35) * mm, "end": v(342.98, 393.58) * mm});
            skLineSegment(sketch, "E459", {"start": v(342.98, 393.58) * mm, "end": v(336.83, 390.78) * mm});
            skLineSegment(sketch, "E460", {"start": v(336.83, 390.78) * mm, "end": v(331.28, 388.03) * mm});
            skLineSegment(sketch, "E461", {"start": v(331.28, 388.03) * mm, "end": v(326.19, 385.33) * mm});
            skLineSegment(sketch, "E462", {"start": v(326.19, 385.33) * mm, "end": v(321.62, 382.61) * mm});
            skLineSegment(sketch, "E463", {"start": v(321.62, 382.61) * mm, "end": v(317.48, 380.08) * mm});
            skLineSegment(sketch, "E464", {"start": v(317.48, 380.08) * mm, "end": v(313.87, 377.68) * mm});
            skLineSegment(sketch, "E465", {"start": v(313.87, 377.68) * mm, "end": v(310.62, 375.4) * mm});
            skLineSegment(sketch, "E466", {"start": v(310.62, 375.4) * mm, "end": v(307.88, 373.23) * mm});
            skLineSegment(sketch, "E467", {"start": v(307.88, 373.23) * mm, "end": v(305.57, 371.41) * mm});
            skLineSegment(sketch, "E468", {"start": v(305.57, 371.41) * mm, "end": v(303.62, 369.7) * mm});
            skLineSegment(sketch, "E469", {"start": v(303.62, 369.7) * mm, "end": v(302.1, 368.34) * mm});
            skLineSegment(sketch, "E470", {"start": v(302.1, 368.34) * mm, "end": v(300.92, 367.24) * mm});
            skLineSegment(sketch, "E471", {"start": v(300.92, 367.24) * mm, "end": v(300.1, 366.4) * mm});
            skLineSegment(sketch, "E472", {"start": v(300.1, 366.4) * mm, "end": v(299.42, 365.58) * mm});
            skLineSegment(sketch, "E473", {"start": v(299.42, 365.58) * mm, "end": v(264.47, 322.91) * mm});
            skArc(sketch, "E474", {"start": v(399.54, 120.77) * mm, "mid": v(376.56, 102.85) * mm, "end": v(371.58, 74.15) * mm});
            skLineSegment(sketch, "E475", {"start": v(399.54, 120.77) * mm, "end": v(452.34, 136.72) * mm});
            skLineSegment(sketch, "E476", {"start": v(452.34, 136.72) * mm, "end": v(453.35, 137.03) * mm});
            skLineSegment(sketch, "E477", {"start": v(453.35, 137.03) * mm, "end": v(454.44, 137.47) * mm});
            skLineSegment(sketch, "E478", {"start": v(454.44, 137.47) * mm, "end": v(455.91, 138.14) * mm});
            skLineSegment(sketch, "E479", {"start": v(455.91, 138.14) * mm, "end": v(457.75, 139.03) * mm});
            skLineSegment(sketch, "E480", {"start": v(457.75, 139.03) * mm, "end": v(460.07, 140.17) * mm});
            skLineSegment(sketch, "E481", {"start": v(460.07, 140.17) * mm, "end": v(462.64, 141.62) * mm});
            skLineSegment(sketch, "E482", {"start": v(462.64, 141.62) * mm, "end": v(465.68, 143.32) * mm});
            skLineSegment(sketch, "E483", {"start": v(465.68, 143.32) * mm, "end": v(469.04, 145.44) * mm});
            skLineSegment(sketch, "E484", {"start": v(469.04, 145.44) * mm, "end": v(472.65, 147.86) * mm});
            skLineSegment(sketch, "E485", {"start": v(472.65, 147.86) * mm, "end": v(476.56, 150.72) * mm});
            skLineSegment(sketch, "E486", {"start": v(476.56, 150.72) * mm, "end": v(480.83, 153.9) * mm});
            skLineSegment(sketch, "E487", {"start": v(480.83, 153.9) * mm, "end": v(485.27, 157.57) * mm});
            skLineSegment(sketch, "E488", {"start": v(485.27, 157.57) * mm, "end": v(489.93, 161.65) * mm});
            skLineSegment(sketch, "E489", {"start": v(489.93, 161.65) * mm, "end": v(494.88, 166.26) * mm});
            skLineSegment(sketch, "E490", {"start": v(494.88, 166.26) * mm, "end": v(499.93, 171.23) * mm});
            skLineSegment(sketch, "E491", {"start": v(499.93, 171.23) * mm, "end": v(505.17, 176.7) * mm});
            skLineSegment(sketch, "E492", {"start": v(505.17, 176.7) * mm, "end": v(510.59, 182.68) * mm});
            skLineSegment(sketch, "E493", {"start": v(510.59, 182.68) * mm, "end": v(516.06, 189.22) * mm});
            skLineSegment(sketch, "E494", {"start": v(516.06, 189.22) * mm, "end": v(521.6, 196.24) * mm});
            skLineSegment(sketch, "E495", {"start": v(521.6, 196.24) * mm, "end": v(525.42, 201.4) * mm});
            skArc(sketch, "E496", {"start": v(525.42, 201.4) * mm, "mid": v(526.42, 203.92) * mm, "end": v(526.06, 206.6) * mm});
            skLineSegment(sketch, "E497", {"start": v(526.06, 206.6) * mm, "end": v(518.07, 225.9) * mm});
            skArc(sketch, "E498", {"start": v(518.07, 225.9) * mm, "mid": v(516.43, 228.05) * mm, "end": v(513.94, 229.12) * mm});
            skLineSegment(sketch, "E499", {"start": v(513.94, 229.12) * mm, "end": v(507.6, 230.07) * mm});
            skLineSegment(sketch, "E500", {"start": v(507.6, 230.07) * mm, "end": v(498.7, 231.1) * mm});
            skLineSegment(sketch, "E501", {"start": v(498.7, 231.1) * mm, "end": v(490.21, 231.87) * mm});
            skLineSegment(sketch, "E502", {"start": v(490.21, 231.87) * mm, "end": v(482.16, 232.26) * mm});
            skLineSegment(sketch, "E503", {"start": v(482.16, 232.26) * mm, "end": v(474.58, 232.43) * mm});
            skLineSegment(sketch, "E504", {"start": v(474.58, 232.43) * mm, "end": v(467.5, 232.37) * mm});
            skLineSegment(sketch, "E505", {"start": v(467.5, 232.37) * mm, "end": v(460.74, 232.13) * mm});
            skLineSegment(sketch, "E506", {"start": v(460.74, 232.13) * mm, "end": v(454.56, 231.72) * mm});
            skLineSegment(sketch, "E507", {"start": v(454.56, 231.72) * mm, "end": v(448.82, 231.18) * mm});
            skLineSegment(sketch, "E508", {"start": v(448.82, 231.18) * mm, "end": v(443.55, 230.4) * mm});
            skLineSegment(sketch, "E509", {"start": v(443.55, 230.4) * mm, "end": v(438.77, 229.65) * mm});
            skLineSegment(sketch, "E510", {"start": v(438.77, 229.65) * mm, "end": v(434.5, 228.82) * mm});
            skLineSegment(sketch, "E511", {"start": v(434.5, 228.82) * mm, "end": v(430.63, 227.95) * mm});
            skLineSegment(sketch, "E512", {"start": v(430.63, 227.95) * mm, "end": v(427.27, 227) * mm});
            skLineSegment(sketch, "E513", {"start": v(427.27, 227) * mm, "end": v(424.44, 226.2) * mm});
            skLineSegment(sketch, "E514", {"start": v(424.44, 226.2) * mm, "end": v(421.99, 225.37) * mm});
            skLineSegment(sketch, "E515", {"start": v(421.99, 225.37) * mm, "end": v(420.06, 224.7) * mm});
            skLineSegment(sketch, "E516", {"start": v(420.06, 224.7) * mm, "end": v(418.55, 224.13) * mm});
            skLineSegment(sketch, "E517", {"start": v(418.55, 224.13) * mm, "end": v(417.47, 223.67) * mm});
            skLineSegment(sketch, "E518", {"start": v(417.47, 223.67) * mm, "end": v(416.53, 223.17) * mm});
            skLineSegment(sketch, "E519", {"start": v(416.53, 223.17) * mm, "end": v(367.91, 197.12) * mm});
            skArc(sketch, "E520", {"start": v(371.67, 73.7) * mm, "mid": v(387.26, 49.08) * mm, "end": v(415.34, 41.32) * mm});
            skLineSegment(sketch, "E521", {"start": v(-264.47, 322.91) * mm, "end": v(-299.42, 365.58) * mm});
            skLineSegment(sketch, "E522", {"start": v(-299.42, 365.58) * mm, "end": v(-300.1, 366.4) * mm});
            skLineSegment(sketch, "E523", {"start": v(-300.1, 366.4) * mm, "end": v(-300.92, 367.24) * mm});
            skLineSegment(sketch, "E524", {"start": v(-300.92, 367.24) * mm, "end": v(-302.1, 368.34) * mm});
            skLineSegment(sketch, "E525", {"start": v(-302.1, 368.34) * mm, "end": v(-303.62, 369.7) * mm});
            skLineSegment(sketch, "E526", {"start": v(-303.62, 369.7) * mm, "end": v(-305.57, 371.41) * mm});
            skLineSegment(sketch, "E527", {"start": v(-305.57, 371.41) * mm, "end": v(-307.88, 373.23) * mm});
            skLineSegment(sketch, "E528", {"start": v(-307.88, 373.23) * mm, "end": v(-310.62, 375.4) * mm});
            skLineSegment(sketch, "E529", {"start": v(-310.62, 375.4) * mm, "end": v(-313.87, 377.68) * mm});
            skLineSegment(sketch, "E530", {"start": v(-313.87, 377.68) * mm, "end": v(-317.48, 380.08) * mm});
            skLineSegment(sketch, "E531", {"start": v(-317.48, 380.08) * mm, "end": v(-321.62, 382.61) * mm});
            skLineSegment(sketch, "E532", {"start": v(-321.62, 382.61) * mm, "end": v(-326.19, 385.33) * mm});
            skLineSegment(sketch, "E533", {"start": v(-326.19, 385.33) * mm, "end": v(-331.28, 388.03) * mm});
            skLineSegment(sketch, "E534", {"start": v(-331.28, 388.03) * mm, "end": v(-336.83, 390.78) * mm});
            skLineSegment(sketch, "E535", {"start": v(-336.83, 390.78) * mm, "end": v(-342.98, 393.58) * mm});
            skLineSegment(sketch, "E536", {"start": v(-342.98, 393.58) * mm, "end": v(-349.51, 396.35) * mm});
            skLineSegment(sketch, "E537", {"start": v(-349.51, 396.35) * mm, "end": v(-356.57, 399.1) * mm});
            skLineSegment(sketch, "E538", {"start": v(-356.57, 399.1) * mm, "end": v(-364.17, 401.81) * mm});
            skLineSegment(sketch, "E539", {"start": v(-364.17, 401.81) * mm, "end": v(-372.3, 404.36) * mm});
            skLineSegment(sketch, "E540", {"start": v(-372.3, 404.36) * mm, "end": v(-380.9, 406.8) * mm});
            skLineSegment(sketch, "E541", {"start": v(-380.9, 406.8) * mm, "end": v(-387.14, 408.35) * mm});
            skArc(sketch, "E542", {"start": v(-387.14, 408.35) * mm, "mid": v(-389.85, 408.32) * mm, "end": v(-392.18, 406.95) * mm});
            skLineSegment(sketch, "E543", {"start": v(-392.18, 406.95) * mm, "end": v(-406.95, 392.18) * mm});
            skArc(sketch, "E544", {"start": v(-406.95, 392.18) * mm, "mid": v(-408.32, 389.85) * mm, "end": v(-408.35, 387.14) * mm});
            skLineSegment(sketch, "E545", {"start": v(-408.35, 387.14) * mm, "end": v(-406.8, 380.9) * mm});
            skLineSegment(sketch, "E546", {"start": v(-406.8, 380.9) * mm, "end": v(-404.36, 372.3) * mm});
            skLineSegment(sketch, "E547", {"start": v(-404.36, 372.3) * mm, "end": v(-401.81, 364.17) * mm});
            skLineSegment(sketch, "E548", {"start": v(-401.81, 364.17) * mm, "end": v(-399.1, 356.57) * mm});
            skLineSegment(sketch, "E549", {"start": v(-399.1, 356.57) * mm, "end": v(-396.35, 349.51) * mm});
            skLineSegment(sketch, "E550", {"start": v(-396.35, 349.51) * mm, "end": v(-393.58, 342.98) * mm});
            skLineSegment(sketch, "E551", {"start": v(-393.58, 342.98) * mm, "end": v(-390.78, 336.83) * mm});
            skLineSegment(sketch, "E552", {"start": v(-390.78, 336.83) * mm, "end": v(-388.03, 331.28) * mm});
            skLineSegment(sketch, "E553", {"start": v(-388.03, 331.28) * mm, "end": v(-385.33, 326.19) * mm});
            skLineSegment(sketch, "E554", {"start": v(-385.33, 326.19) * mm, "end": v(-382.61, 321.62) * mm});
            skLineSegment(sketch, "E555", {"start": v(-382.61, 321.62) * mm, "end": v(-380.08, 317.48) * mm});
            skLineSegment(sketch, "E556", {"start": v(-380.08, 317.48) * mm, "end": v(-377.68, 313.87) * mm});
            skLineSegment(sketch, "E557", {"start": v(-377.68, 313.87) * mm, "end": v(-375.4, 310.62) * mm});
            skLineSegment(sketch, "E558", {"start": v(-375.4, 310.62) * mm, "end": v(-373.23, 307.88) * mm});
            skLineSegment(sketch, "E559", {"start": v(-373.23, 307.88) * mm, "end": v(-371.41, 305.57) * mm});
            skLineSegment(sketch, "E560", {"start": v(-371.41, 305.57) * mm, "end": v(-369.7, 303.62) * mm});
            skLineSegment(sketch, "E561", {"start": v(-369.7, 303.62) * mm, "end": v(-368.34, 302.1) * mm});
            skLineSegment(sketch, "E562", {"start": v(-368.34, 302.1) * mm, "end": v(-367.24, 300.92) * mm});
            skLineSegment(sketch, "E563", {"start": v(-367.24, 300.92) * mm, "end": v(-366.4, 300.1) * mm});
            skLineSegment(sketch, "E564", {"start": v(-366.4, 300.1) * mm, "end": v(-365.58, 299.42) * mm});
            skLineSegment(sketch, "E565", {"start": v(-365.58, 299.42) * mm, "end": v(-322.91, 264.47) * mm});
            skArc(sketch, "E566", {"start": v(-120.77, 399.54) * mm, "mid": v(-102.85, 376.56) * mm, "end": v(-74.15, 371.58) * mm});
            skLineSegment(sketch, "E567", {"start": v(-120.77, 399.54) * mm, "end": v(-136.72, 452.34) * mm});
            skLineSegment(sketch, "E568", {"start": v(-136.72, 452.34) * mm, "end": v(-137.03, 453.35) * mm});
            skLineSegment(sketch, "E569", {"start": v(-137.03, 453.35) * mm, "end": v(-137.47, 454.44) * mm});
            skLineSegment(sketch, "E570", {"start": v(-137.47, 454.44) * mm, "end": v(-138.14, 455.91) * mm});
            skLineSegment(sketch, "E571", {"start": v(-138.14, 455.91) * mm, "end": v(-139.03, 457.75) * mm});
            skLineSegment(sketch, "E572", {"start": v(-139.03, 457.75) * mm, "end": v(-140.17, 460.07) * mm});
            skLineSegment(sketch, "E573", {"start": v(-140.17, 460.07) * mm, "end": v(-141.62, 462.64) * mm});
            skLineSegment(sketch, "E574", {"start": v(-141.62, 462.64) * mm, "end": v(-143.32, 465.68) * mm});
            skLineSegment(sketch, "E575", {"start": v(-143.32, 465.68) * mm, "end": v(-145.44, 469.04) * mm});
            skLineSegment(sketch, "E576", {"start": v(-145.44, 469.04) * mm, "end": v(-147.86, 472.65) * mm});
            skLineSegment(sketch, "E577", {"start": v(-147.86, 472.65) * mm, "end": v(-150.72, 476.56) * mm});
            skLineSegment(sketch, "E578", {"start": v(-150.72, 476.56) * mm, "end": v(-153.9, 480.83) * mm});
            skLineSegment(sketch, "E579", {"start": v(-153.9, 480.83) * mm, "end": v(-157.57, 485.27) * mm});
            skLineSegment(sketch, "E580", {"start": v(-157.57, 485.27) * mm, "end": v(-161.65, 489.93) * mm});
            skLineSegment(sketch, "E581", {"start": v(-161.65, 489.93) * mm, "end": v(-166.26, 494.88) * mm});
            skLineSegment(sketch, "E582", {"start": v(-166.26, 494.88) * mm, "end": v(-171.23, 499.93) * mm});
            skLineSegment(sketch, "E583", {"start": v(-171.23, 499.93) * mm, "end": v(-176.7, 505.17) * mm});
            skLineSegment(sketch, "E584", {"start": v(-176.7, 505.17) * mm, "end": v(-182.68, 510.59) * mm});
            skLineSegment(sketch, "E585", {"start": v(-182.68, 510.59) * mm, "end": v(-189.22, 516.06) * mm});
            skLineSegment(sketch, "E586", {"start": v(-189.22, 516.06) * mm, "end": v(-196.24, 521.6) * mm});
            skLineSegment(sketch, "E587", {"start": v(-196.24, 521.6) * mm, "end": v(-201.4, 525.42) * mm});
            skArc(sketch, "E588", {"start": v(-201.4, 525.42) * mm, "mid": v(-203.92, 526.42) * mm, "end": v(-206.6, 526.06) * mm});
            skLineSegment(sketch, "E589", {"start": v(-206.6, 526.06) * mm, "end": v(-225.9, 518.07) * mm});
            skArc(sketch, "E590", {"start": v(-225.9, 518.07) * mm, "mid": v(-228.05, 516.43) * mm, "end": v(-229.12, 513.94) * mm});
            skLineSegment(sketch, "E591", {"start": v(-229.12, 513.94) * mm, "end": v(-230.07, 507.6) * mm});
            skLineSegment(sketch, "E592", {"start": v(-230.07, 507.6) * mm, "end": v(-231.1, 498.7) * mm});
            skLineSegment(sketch, "E593", {"start": v(-231.1, 498.7) * mm, "end": v(-231.87, 490.21) * mm});
            skLineSegment(sketch, "E594", {"start": v(-231.87, 490.21) * mm, "end": v(-232.26, 482.16) * mm});
            skLineSegment(sketch, "E595", {"start": v(-232.26, 482.16) * mm, "end": v(-232.43, 474.58) * mm});
            skLineSegment(sketch, "E596", {"start": v(-232.43, 474.58) * mm, "end": v(-232.37, 467.5) * mm});
            skLineSegment(sketch, "E597", {"start": v(-232.37, 467.5) * mm, "end": v(-232.13, 460.74) * mm});
            skLineSegment(sketch, "E598", {"start": v(-232.13, 460.74) * mm, "end": v(-231.72, 454.56) * mm});
            skLineSegment(sketch, "E599", {"start": v(-231.72, 454.56) * mm, "end": v(-231.18, 448.82) * mm});
            skLineSegment(sketch, "E600", {"start": v(-231.18, 448.82) * mm, "end": v(-230.4, 443.55) * mm});
            skLineSegment(sketch, "E601", {"start": v(-230.4, 443.55) * mm, "end": v(-229.65, 438.77) * mm});
            skLineSegment(sketch, "E602", {"start": v(-229.65, 438.77) * mm, "end": v(-228.82, 434.5) * mm});
            skLineSegment(sketch, "E603", {"start": v(-228.82, 434.5) * mm, "end": v(-227.95, 430.63) * mm});
            skLineSegment(sketch, "E604", {"start": v(-227.95, 430.63) * mm, "end": v(-227, 427.27) * mm});
            skLineSegment(sketch, "E605", {"start": v(-227, 427.27) * mm, "end": v(-226.2, 424.44) * mm});
            skLineSegment(sketch, "E606", {"start": v(-226.2, 424.44) * mm, "end": v(-225.37, 421.99) * mm});
            skLineSegment(sketch, "E607", {"start": v(-225.37, 421.99) * mm, "end": v(-224.7, 420.06) * mm});
            skLineSegment(sketch, "E608", {"start": v(-224.7, 420.06) * mm, "end": v(-224.13, 418.55) * mm});
            skLineSegment(sketch, "E609", {"start": v(-224.13, 418.55) * mm, "end": v(-223.67, 417.47) * mm});
            skLineSegment(sketch, "E610", {"start": v(-223.67, 417.47) * mm, "end": v(-223.17, 416.53) * mm});
            skLineSegment(sketch, "E611", {"start": v(-223.17, 416.53) * mm, "end": v(-197.12, 367.91) * mm});
            skArc(sketch, "E612", {"start": v(-73.7, 371.67) * mm, "mid": v(-49.08, 387.26) * mm, "end": v(-41.32, 415.34) * mm});
            skArc(sketch, "E613", {"start": v(41.32, 415.34) * mm, "mid": v(49.08, 387.26) * mm, "end": v(73.7, 371.67) * mm});
            skArc(sketch, "E614", {"start": v(74.15, 371.58) * mm, "mid": v(102.85, 376.56) * mm, "end": v(120.77, 399.54) * mm});
            skLineSegment(sketch, "E615", {"start": v(197.12, 367.91) * mm, "end": v(223.17, 416.53) * mm});
            skLineSegment(sketch, "E616", {"start": v(223.17, 416.53) * mm, "end": v(223.67, 417.47) * mm});
            skLineSegment(sketch, "E617", {"start": v(223.67, 417.47) * mm, "end": v(224.13, 418.55) * mm});
            skLineSegment(sketch, "E618", {"start": v(224.13, 418.55) * mm, "end": v(224.7, 420.06) * mm});
            skLineSegment(sketch, "E619", {"start": v(224.7, 420.06) * mm, "end": v(225.37, 421.99) * mm});
            skLineSegment(sketch, "E620", {"start": v(225.37, 421.99) * mm, "end": v(226.2, 424.44) * mm});
            skLineSegment(sketch, "E621", {"start": v(226.2, 424.44) * mm, "end": v(227, 427.27) * mm});
            skLineSegment(sketch, "E622", {"start": v(227, 427.27) * mm, "end": v(227.95, 430.63) * mm});
            skLineSegment(sketch, "E623", {"start": v(227.95, 430.63) * mm, "end": v(228.82, 434.5) * mm});
            skLineSegment(sketch, "E624", {"start": v(228.82, 434.5) * mm, "end": v(229.65, 438.77) * mm});
            skLineSegment(sketch, "E625", {"start": v(229.65, 438.77) * mm, "end": v(230.4, 443.55) * mm});
            skLineSegment(sketch, "E626", {"start": v(230.4, 443.55) * mm, "end": v(231.18, 448.82) * mm});
            skLineSegment(sketch, "E627", {"start": v(231.18, 448.82) * mm, "end": v(231.72, 454.56) * mm});
            skLineSegment(sketch, "E628", {"start": v(231.72, 454.56) * mm, "end": v(232.13, 460.74) * mm});
            skLineSegment(sketch, "E629", {"start": v(232.13, 460.74) * mm, "end": v(232.37, 467.5) * mm});
            skLineSegment(sketch, "E630", {"start": v(232.37, 467.5) * mm, "end": v(232.43, 474.58) * mm});
            skLineSegment(sketch, "E631", {"start": v(232.43, 474.58) * mm, "end": v(232.26, 482.16) * mm});
            skLineSegment(sketch, "E632", {"start": v(232.26, 482.16) * mm, "end": v(231.87, 490.21) * mm});
            skLineSegment(sketch, "E633", {"start": v(231.87, 490.21) * mm, "end": v(231.1, 498.7) * mm});
            skLineSegment(sketch, "E634", {"start": v(231.1, 498.7) * mm, "end": v(230.07, 507.6) * mm});
            skLineSegment(sketch, "E635", {"start": v(230.07, 507.6) * mm, "end": v(229.12, 513.94) * mm});
            skArc(sketch, "E636", {"start": v(229.12, 513.94) * mm, "mid": v(228.05, 516.43) * mm, "end": v(225.9, 518.07) * mm});
            skLineSegment(sketch, "E637", {"start": v(225.9, 518.07) * mm, "end": v(206.6, 526.06) * mm});
            skArc(sketch, "E638", {"start": v(206.6, 526.06) * mm, "mid": v(203.92, 526.42) * mm, "end": v(201.4, 525.42) * mm});
            skLineSegment(sketch, "E639", {"start": v(201.4, 525.42) * mm, "end": v(196.24, 521.6) * mm});
            skLineSegment(sketch, "E640", {"start": v(196.24, 521.6) * mm, "end": v(189.22, 516.06) * mm});
            skLineSegment(sketch, "E641", {"start": v(189.22, 516.06) * mm, "end": v(182.68, 510.59) * mm});
            skLineSegment(sketch, "E642", {"start": v(182.68, 510.59) * mm, "end": v(176.7, 505.17) * mm});
            skLineSegment(sketch, "E643", {"start": v(176.7, 505.17) * mm, "end": v(171.23, 499.93) * mm});
            skLineSegment(sketch, "E644", {"start": v(171.23, 499.93) * mm, "end": v(166.26, 494.88) * mm});
            skLineSegment(sketch, "E645", {"start": v(166.26, 494.88) * mm, "end": v(161.65, 489.93) * mm});
            skLineSegment(sketch, "E646", {"start": v(161.65, 489.93) * mm, "end": v(157.57, 485.27) * mm});
            skLineSegment(sketch, "E647", {"start": v(157.57, 485.27) * mm, "end": v(153.9, 480.83) * mm});
            skLineSegment(sketch, "E648", {"start": v(153.9, 480.83) * mm, "end": v(150.72, 476.56) * mm});
            skLineSegment(sketch, "E649", {"start": v(150.72, 476.56) * mm, "end": v(147.86, 472.65) * mm});
            skLineSegment(sketch, "E650", {"start": v(147.86, 472.65) * mm, "end": v(145.44, 469.04) * mm});
            skLineSegment(sketch, "E651", {"start": v(145.44, 469.04) * mm, "end": v(143.32, 465.68) * mm});
            skLineSegment(sketch, "E652", {"start": v(143.32, 465.68) * mm, "end": v(141.62, 462.64) * mm});
            skLineSegment(sketch, "E653", {"start": v(141.62, 462.64) * mm, "end": v(140.17, 460.07) * mm});
            skLineSegment(sketch, "E654", {"start": v(140.17, 460.07) * mm, "end": v(139.03, 457.75) * mm});
            skLineSegment(sketch, "E655", {"start": v(139.03, 457.75) * mm, "end": v(138.14, 455.91) * mm});
            skLineSegment(sketch, "E656", {"start": v(138.14, 455.91) * mm, "end": v(137.47, 454.44) * mm});
            skLineSegment(sketch, "E657", {"start": v(137.47, 454.44) * mm, "end": v(137.03, 453.35) * mm});
            skLineSegment(sketch, "E658", {"start": v(137.03, 453.35) * mm, "end": v(136.72, 452.34) * mm});
            skLineSegment(sketch, "E659", {"start": v(136.72, 452.34) * mm, "end": v(120.77, 399.54) * mm});
            skLineSegment(sketch, "E660", {"start": v(-367.91, 197.12) * mm, "end": v(-416.53, 223.17) * mm});
            skLineSegment(sketch, "E661", {"start": v(-416.53, 223.17) * mm, "end": v(-417.47, 223.67) * mm});
            skLineSegment(sketch, "E662", {"start": v(-417.47, 223.67) * mm, "end": v(-418.55, 224.13) * mm});
            skLineSegment(sketch, "E663", {"start": v(-418.55, 224.13) * mm, "end": v(-420.06, 224.7) * mm});
            skLineSegment(sketch, "E664", {"start": v(-420.06, 224.7) * mm, "end": v(-421.99, 225.37) * mm});
            skLineSegment(sketch, "E665", {"start": v(-421.99, 225.37) * mm, "end": v(-424.44, 226.2) * mm});
            skLineSegment(sketch, "E666", {"start": v(-424.44, 226.2) * mm, "end": v(-427.27, 227) * mm});
            skLineSegment(sketch, "E667", {"start": v(-427.27, 227) * mm, "end": v(-430.63, 227.95) * mm});
            skLineSegment(sketch, "E668", {"start": v(-430.63, 227.95) * mm, "end": v(-434.5, 228.82) * mm});
            skLineSegment(sketch, "E669", {"start": v(-434.5, 228.82) * mm, "end": v(-438.77, 229.65) * mm});
            skLineSegment(sketch, "E670", {"start": v(-438.77, 229.65) * mm, "end": v(-443.55, 230.4) * mm});
            skLineSegment(sketch, "E671", {"start": v(-443.55, 230.4) * mm, "end": v(-448.82, 231.18) * mm});
            skLineSegment(sketch, "E672", {"start": v(-448.82, 231.18) * mm, "end": v(-454.56, 231.72) * mm});
            skLineSegment(sketch, "E673", {"start": v(-454.56, 231.72) * mm, "end": v(-460.74, 232.13) * mm});
            skLineSegment(sketch, "E674", {"start": v(-460.74, 232.13) * mm, "end": v(-467.5, 232.37) * mm});
            skLineSegment(sketch, "E675", {"start": v(-467.5, 232.37) * mm, "end": v(-474.58, 232.43) * mm});
            skLineSegment(sketch, "E676", {"start": v(-474.58, 232.43) * mm, "end": v(-482.16, 232.26) * mm});
            skLineSegment(sketch, "E677", {"start": v(-482.16, 232.26) * mm, "end": v(-490.21, 231.87) * mm});
            skLineSegment(sketch, "E678", {"start": v(-490.21, 231.87) * mm, "end": v(-498.7, 231.1) * mm});
            skLineSegment(sketch, "E679", {"start": v(-498.7, 231.1) * mm, "end": v(-507.6, 230.07) * mm});
            skLineSegment(sketch, "E680", {"start": v(-507.6, 230.07) * mm, "end": v(-513.94, 229.12) * mm});
            skArc(sketch, "E681", {"start": v(-513.94, 229.12) * mm, "mid": v(-516.43, 228.05) * mm, "end": v(-518.07, 225.9) * mm});
            skLineSegment(sketch, "E682", {"start": v(-518.07, 225.9) * mm, "end": v(-526.06, 206.6) * mm});
            skArc(sketch, "E683", {"start": v(-526.06, 206.6) * mm, "mid": v(-526.42, 203.92) * mm, "end": v(-525.42, 201.4) * mm});
            skLineSegment(sketch, "E684", {"start": v(-525.42, 201.4) * mm, "end": v(-521.6, 196.24) * mm});
            skLineSegment(sketch, "E685", {"start": v(-521.6, 196.24) * mm, "end": v(-516.06, 189.22) * mm});
            skLineSegment(sketch, "E686", {"start": v(-516.06, 189.22) * mm, "end": v(-510.59, 182.68) * mm});
            skLineSegment(sketch, "E687", {"start": v(-510.59, 182.68) * mm, "end": v(-505.17, 176.7) * mm});
            skLineSegment(sketch, "E688", {"start": v(-505.17, 176.7) * mm, "end": v(-499.93, 171.23) * mm});
            skLineSegment(sketch, "E689", {"start": v(-499.93, 171.23) * mm, "end": v(-494.88, 166.26) * mm});
            skLineSegment(sketch, "E690", {"start": v(-494.88, 166.26) * mm, "end": v(-489.93, 161.65) * mm});
            skLineSegment(sketch, "E691", {"start": v(-489.93, 161.65) * mm, "end": v(-485.27, 157.57) * mm});
            skLineSegment(sketch, "E692", {"start": v(-485.27, 157.57) * mm, "end": v(-480.83, 153.9) * mm});
            skLineSegment(sketch, "E693", {"start": v(-480.83, 153.9) * mm, "end": v(-476.56, 150.72) * mm});
            skLineSegment(sketch, "E694", {"start": v(-476.56, 150.72) * mm, "end": v(-472.65, 147.86) * mm});
            skLineSegment(sketch, "E695", {"start": v(-472.65, 147.86) * mm, "end": v(-469.04, 145.44) * mm});
            skLineSegment(sketch, "E696", {"start": v(-469.04, 145.44) * mm, "end": v(-465.68, 143.32) * mm});
            skLineSegment(sketch, "E697", {"start": v(-465.68, 143.32) * mm, "end": v(-462.64, 141.62) * mm});
            skLineSegment(sketch, "E698", {"start": v(-462.64, 141.62) * mm, "end": v(-460.07, 140.17) * mm});
            skLineSegment(sketch, "E699", {"start": v(-460.07, 140.17) * mm, "end": v(-457.75, 139.03) * mm});
            skLineSegment(sketch, "E700", {"start": v(-457.75, 139.03) * mm, "end": v(-455.91, 138.14) * mm});
            skLineSegment(sketch, "E701", {"start": v(-455.91, 138.14) * mm, "end": v(-454.44, 137.47) * mm});
            skLineSegment(sketch, "E702", {"start": v(-454.44, 137.47) * mm, "end": v(-453.35, 137.03) * mm});
            skLineSegment(sketch, "E703", {"start": v(-453.35, 137.03) * mm, "end": v(-452.34, 136.72) * mm});
            skLineSegment(sketch, "E704", {"start": v(-452.34, 136.72) * mm, "end": v(-399.54, 120.77) * mm});
            skArc(sketch, "E705", {"start": v(-367.91, 197.12) * mm, "mid": v(-339, 193.54) * mm, "end": v(-315.18, 210.32) * mm});
            skArc(sketch, "E706", {"start": v(315.18, 210.32) * mm, "mid": v(339, 193.54) * mm, "end": v(367.91, 197.12) * mm});
            skArc(sketch, "E707", {"start": v(-371.58, 74.15) * mm, "mid": v(-376.56, 102.85) * mm, "end": v(-399.54, 120.77) * mm});
            skArc(sketch, "E708", {"start": v(-415.34, 41.32) * mm, "mid": v(-387.26, 49.08) * mm, "end": v(-371.67, 73.7) * mm});
            skLineSegment(sketch, "E709", {"start": v(-371.67, 73.7) * mm, "end": v(-371.58, 74.15) * mm});
            skLineSegment(sketch, "E710", {"start": v(371.58, 74.15) * mm, "end": v(371.67, 73.7) * mm});
            skArc(sketch, "E711", {"start": v(-314.92, 210.7) * mm, "mid": v(-308.53, 239.13) * mm, "end": v(-322.91, 264.47) * mm});
            skLineSegment(sketch, "E712", {"start": v(-315.18, 210.32) * mm, "end": v(-314.92, 210.7) * mm});
            skArc(sketch, "E713", {"start": v(-264.47, 322.91) * mm, "mid": v(-239.13, 308.53) * mm, "end": v(-210.7, 314.92) * mm});
            skArc(sketch, "E714", {"start": v(-210.32, 315.18) * mm, "mid": v(-193.54, 339) * mm, "end": v(-197.12, 367.91) * mm});
            skLineSegment(sketch, "E715", {"start": v(-210.7, 314.92) * mm, "end": v(-210.32, 315.18) * mm});
            skLineSegment(sketch, "E716", {"start": v(-74.15, 371.58) * mm, "end": v(-73.7, 371.67) * mm});
            skArc(sketch, "E717", {"start": v(322.91, 264.47) * mm, "mid": v(308.53, 239.13) * mm, "end": v(314.92, 210.7) * mm});
            skLineSegment(sketch, "E718", {"start": v(314.92, 210.7) * mm, "end": v(315.18, 210.32) * mm});
            skLineSegment(sketch, "E719", {"start": v(73.7, 371.67) * mm, "end": v(74.15, 371.58) * mm});
            skArc(sketch, "E720", {"start": v(197.12, 367.91) * mm, "mid": v(193.54, 339) * mm, "end": v(210.32, 315.18) * mm});
            skArc(sketch, "E721", {"start": v(210.7, 314.92) * mm, "mid": v(239.13, 308.53) * mm, "end": v(264.47, 322.91) * mm});
            skLineSegment(sketch, "E722", {"start": v(210.32, 315.18) * mm, "end": v(210.7, 314.92) * mm});
            skLineSegment(sketch, "E723", {"start": v(41.32, 415.34) * mm, "end": v(46.78, 470.23) * mm});
            skLineSegment(sketch, "E724", {"start": v(46.78, 470.23) * mm, "end": v(46.9, 471.28) * mm});
            skLineSegment(sketch, "E725", {"start": v(46.9, 471.28) * mm, "end": v(46.9, 472.46) * mm});
            skLineSegment(sketch, "E726", {"start": v(46.9, 472.46) * mm, "end": v(46.85, 474.07) * mm});
            skLineSegment(sketch, "E727", {"start": v(46.85, 474.07) * mm, "end": v(46.73, 476.11) * mm});
            skLineSegment(sketch, "E728", {"start": v(46.73, 476.11) * mm, "end": v(46.56, 478.7) * mm});
            skLineSegment(sketch, "E729", {"start": v(46.56, 478.7) * mm, "end": v(46.2, 481.62) * mm});
            skLineSegment(sketch, "E730", {"start": v(46.2, 481.62) * mm, "end": v(45.8, 485.08) * mm});
            skLineSegment(sketch, "E731", {"start": v(45.8, 485.08) * mm, "end": v(45.12, 489) * mm});
            skLineSegment(sketch, "E732", {"start": v(45.12, 489) * mm, "end": v(44.26, 493.25) * mm});
            skLineSegment(sketch, "E733", {"start": v(44.26, 493.25) * mm, "end": v(43.13, 497.96) * mm});
            skLineSegment(sketch, "E734", {"start": v(43.13, 497.96) * mm, "end": v(41.82, 503.12) * mm});
            skLineSegment(sketch, "E735", {"start": v(41.82, 503.12) * mm, "end": v(40.13, 508.63) * mm});
            skLineSegment(sketch, "E736", {"start": v(40.13, 508.63) * mm, "end": v(38.14, 514.5) * mm});
            skLineSegment(sketch, "E737", {"start": v(38.14, 514.5) * mm, "end": v(35.78, 520.83) * mm});
            skLineSegment(sketch, "E738", {"start": v(35.78, 520.83) * mm, "end": v(33.12, 527.4) * mm});
            skLineSegment(sketch, "E739", {"start": v(33.12, 527.4) * mm, "end": v(30.07, 534.34) * mm});
            skLineSegment(sketch, "E740", {"start": v(30.07, 534.34) * mm, "end": v(26.62, 541.63) * mm});
            skLineSegment(sketch, "E741", {"start": v(26.62, 541.63) * mm, "end": v(22.67, 549.19) * mm});
            skLineSegment(sketch, "E742", {"start": v(22.67, 549.19) * mm, "end": v(18.31, 557) * mm});
            skLineSegment(sketch, "E743", {"start": v(18.31, 557) * mm, "end": v(15, 562.5) * mm});
            skArc(sketch, "E744", {"start": v(15, 562.5) * mm, "mid": v(13.06, 564.39) * mm, "end": v(10.44, 565.08) * mm});
            skLineSegment(sketch, "E745", {"start": v(10.44, 565.08) * mm, "end": v(-10.44, 565.08) * mm});
            skArc(sketch, "E746", {"start": v(-10.44, 565.08) * mm, "mid": v(-13.06, 564.39) * mm, "end": v(-15, 562.5) * mm});
            skLineSegment(sketch, "E747", {"start": v(-15, 562.5) * mm, "end": v(-18.31, 557) * mm});
            skLineSegment(sketch, "E748", {"start": v(-18.31, 557) * mm, "end": v(-22.67, 549.19) * mm});
            skLineSegment(sketch, "E749", {"start": v(-22.67, 549.19) * mm, "end": v(-26.62, 541.63) * mm});
            skLineSegment(sketch, "E750", {"start": v(-26.62, 541.63) * mm, "end": v(-30.07, 534.34) * mm});
            skLineSegment(sketch, "E751", {"start": v(-30.07, 534.34) * mm, "end": v(-33.12, 527.4) * mm});
            skLineSegment(sketch, "E752", {"start": v(-33.12, 527.4) * mm, "end": v(-35.78, 520.83) * mm});
            skLineSegment(sketch, "E753", {"start": v(-35.78, 520.83) * mm, "end": v(-38.14, 514.5) * mm});
            skLineSegment(sketch, "E754", {"start": v(-38.14, 514.5) * mm, "end": v(-40.13, 508.63) * mm});
            skLineSegment(sketch, "E755", {"start": v(-40.13, 508.63) * mm, "end": v(-41.82, 503.12) * mm});
            skLineSegment(sketch, "E756", {"start": v(-41.82, 503.12) * mm, "end": v(-43.13, 497.96) * mm});
            skLineSegment(sketch, "E757", {"start": v(-43.13, 497.96) * mm, "end": v(-44.26, 493.25) * mm});
            skLineSegment(sketch, "E758", {"start": v(-44.26, 493.25) * mm, "end": v(-45.12, 489) * mm});
            skLineSegment(sketch, "E759", {"start": v(-45.12, 489) * mm, "end": v(-45.8, 485.08) * mm});
            skLineSegment(sketch, "E760", {"start": v(-45.8, 485.08) * mm, "end": v(-46.2, 481.62) * mm});
            skLineSegment(sketch, "E761", {"start": v(-46.2, 481.62) * mm, "end": v(-46.56, 478.7) * mm});
            skLineSegment(sketch, "E762", {"start": v(-46.56, 478.7) * mm, "end": v(-46.73, 476.11) * mm});
            skLineSegment(sketch, "E763", {"start": v(-46.73, 476.11) * mm, "end": v(-46.85, 474.07) * mm});
            skLineSegment(sketch, "E764", {"start": v(-46.85, 474.07) * mm, "end": v(-46.9, 472.46) * mm});
            skLineSegment(sketch, "E765", {"start": v(-46.9, 472.46) * mm, "end": v(-46.9, 471.28) * mm});
            skLineSegment(sketch, "E766", {"start": v(-46.9, 471.28) * mm, "end": v(-46.78, 470.23) * mm});
            skLineSegment(sketch, "E767", {"start": v(-46.78, 470.23) * mm, "end": v(-41.32, 415.34) * mm});
            skArc(sketch, "E768", {"start": v(-38, 238.5) * mm, "mid": v(-170.77, -170.77) * mm, "end": v(238.5, -38) * mm});
            skLineSegment(sketch, "E769", {"start": v(-38, 238.5) * mm, "end": v(-38, 260) * mm});
            skLineSegment(sketch, "E770", {"start": v(38, 238.5) * mm, "end": v(38, 260) * mm});
            skLineSegment(sketch, "E771", {"start": v(238.5, 38) * mm, "end": v(260, 38) * mm});
            skLineSegment(sketch, "E772", {"start": v(238.5, -38) * mm, "end": v(260, -38) * mm});
            skLineSegment(sketch, "E773", {"start": v(38, 260) * mm, "end": v(-38, 260) * mm});
            skLineSegment(sketch, "E774", {"start": v(260, -38) * mm, "end": v(260, 38) * mm});
            skArc(sketch, "E775", {"start": v(238.5, 38) * mm, "mid": v(170.77, 170.77) * mm, "end": v(38, 238.5) * mm});
            skLineSegment(sketch, "E776", {"start": v(0, 0) * mm, "end": v(722.4, 0) * mm, "construction": true});
            skLineSegment(sketch, "E777", {"start": v(0, 0) * mm, "end": v(0, 634.3) * mm, "construction": true});
            skLineSegment(sketch, "E778", {"start": v(0, 0) * mm, "end": v(0, -241.5) * mm, "construction": true});
            skSolve(sketch);
        }
        {
            var Q0;
            Q0=makeQuery(id+"F0.imprint","IMPRINT",FACE,{"disambiguationData":[TD([[makeQuery(id+"F0.imprint","IMPRINT",EDGE,{"derivedFrom":sQuery(id+"F0.wireOp",EDGE,"E0")}),1.0]])]});
            extrude(context, id + "F1", {"entities" : qUnion([Q0]), "endBound" : BoundingType.SYMMETRIC, "depth" : 500 * mm});
        }
        {
            var Q0;
            Q0=qCreatedBy(makeId("Right.planeOp"),FACE);
            var sketch = newSketch(context, id + "F2", { "sketchPlane" : qUnion([Q0])});
            skLineSegment(sketch, "E779.bottom", {"start": v(-50, -241.5) * mm, "end": v(50, -241.5) * mm});
            skLineSegment(sketch, "E779.top", {"start": v(-45, -266.5) * mm, "end": v(45, -266.5) * mm});
            skLineSegment(sketch, "E779.left", {"start": v(-50, -241.5) * mm, "end": v(-50, -261.5) * mm});
            skLineSegment(sketch, "E779.right", {"start": v(50, -241.5) * mm, "end": v(50, -261.5) * mm});
            skPoint(sketch, "E780.visualSharp", {"position": v(-50, -266.5) * mm});
            skArc(sketch, "E780.filletArc", {"start": v(-50, -261.5) * mm, "mid": v(-48.54, -265.04) * mm, "end": v(-45, -266.5) * mm});
            skPoint(sketch, "E781.visualSharp", {"position": v(50, -266.5) * mm});
            skArc(sketch, "E781.filletArc", {"start": v(45, -266.5) * mm, "mid": v(48.54, -265.04) * mm, "end": v(50, -261.5) * mm});
            skSolve(sketch);
        }
        {
            var Q0;
            Q0=makeQuery(id+"F2.imprint","IMPRINT",FACE,{"disambiguationData":[TD([[makeQuery(id+"F2.imprint","IMPRINT",EDGE,{"derivedFrom":sQuery(id+"F2.wireOp",EDGE,"E779.bottom")}),-1.0]])]});
            var Q1;
            Q1=makeQuery(id+"F1.opExtrude","SWEPT_FACE",FACE,{"disambiguationData":[OSD([sQuery(id+"F0.wireOp",EDGE,"E768")])]});
            revolve(context, id + "F3", {"operationType" : NewBodyOperationType.REMOVE, "entities" : qUnion([Q0]), "axis" : qUnion([Q1]), "revolveType" : RevolveType.FULL, "oppositeDirection" : true});
        }
    });
